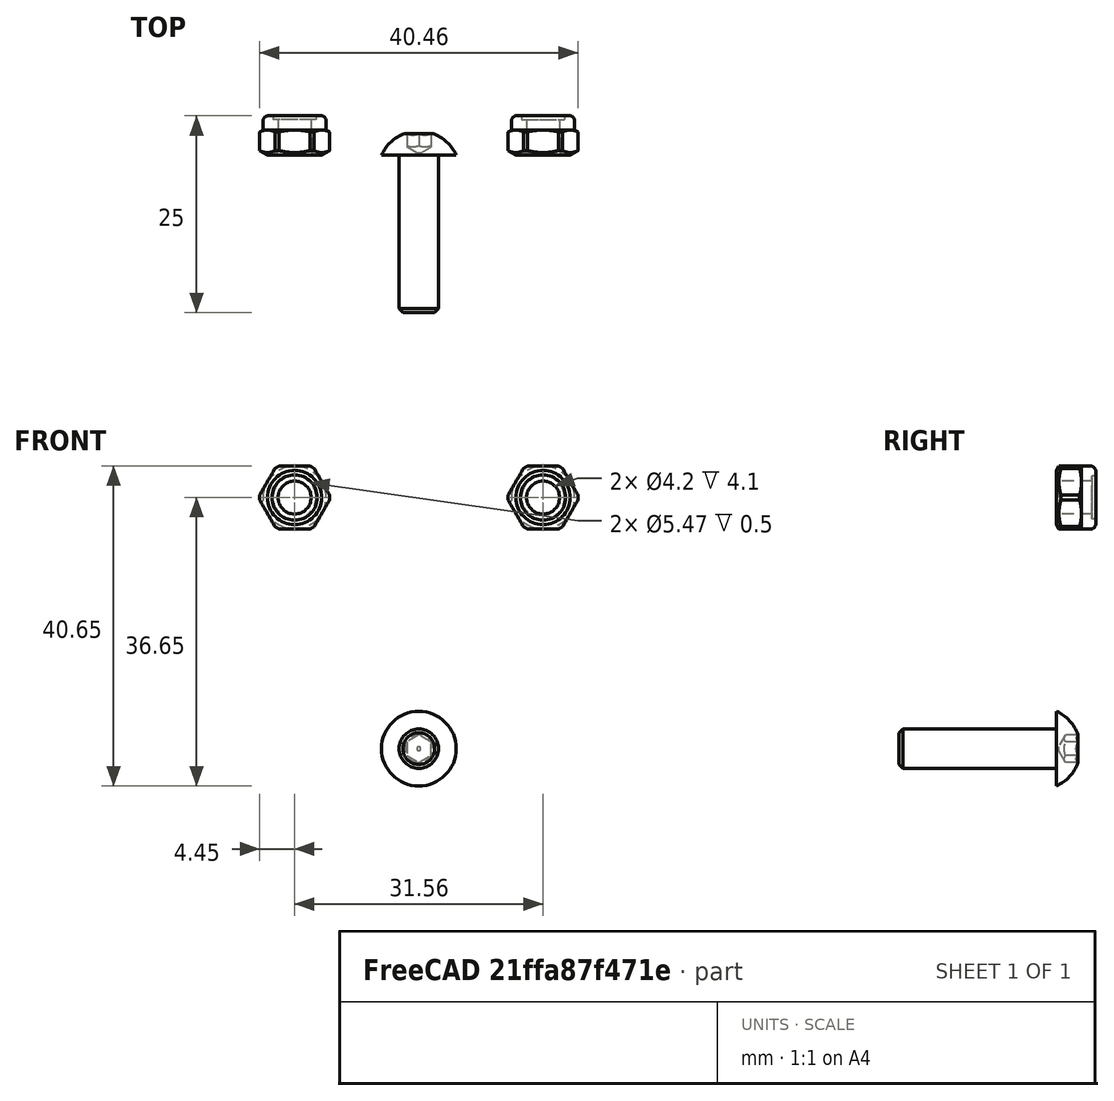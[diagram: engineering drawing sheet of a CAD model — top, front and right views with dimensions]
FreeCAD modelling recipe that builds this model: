
FCSTD DOCUMENT  (FreeCAD 0.19R24267 (Git))
Label: watercooled_print_head
License: All rights reserved
LicenseURL: http://en.wikipedia.org/wiki/All_rights_reserved
objects: App::Link×26, Part::FeaturePython×3, App::DocumentObjectGroup×2, PartDesign::CoordinateSystem×2, App::FeaturePython×1, App::Part×1
note: 5 computed .brp shape members not serialized (recipe doc carries the construction recipe); baked Part::Feature solids carry a one-line shape summary decoded from their .brp
EXTERNAL_REF file=watercooled_block.FCStd obj=LCS_7
EXTERNAL_REF file=watercooled_block.FCStd obj=Part
EXTERNAL_REF file=barb_fitting LC-0640-M6.FCStd obj=LCS_1
EXTERNAL_REF file=watercooled_block.FCStd obj=LCS_4
EXTERNAL_REF file=barb_fitting LC-0640-M6.FCStd obj=Part
EXTERNAL_REF file=watercooled_block.FCStd obj=LCS_5
EXTERNAL_REF file=eccentric_spacer.FCStd obj=LCS_1
EXTERNAL_REF file=watercooled_block.FCStd obj=LCS_9
EXTERNAL_REF file=eccentric_spacer.FCStd obj=Part
EXTERNAL_REF file=watercooled_block.FCStd obj=LCS_10
EXTERNAL_REF file=plug_fitting_MSWZ6.FCStd obj=LCS_1
EXTERNAL_REF file=watercooled_block.FCStd obj=LCS_3
EXTERNAL_REF file=plug_fitting_MSWZ6.FCStd obj=Part
EXTERNAL_REF file=e3d_volcano_assembly.FCStd obj=LCS_Origin
EXTERNAL_REF file=e3d_volcano_assembly.FCStd obj=Model
EXTERNAL_REF file=G5_extruder.FCStd obj=LCS_5
EXTERNAL_REF file=watercooled_block.FCStd obj=LCS_6
EXTERNAL_REF file=G5_extruder.FCStd obj=Model
EXTERNAL_REF file=eccentric_spacer.FCStd obj=LCS_2
EXTERNAL_REF file=precision_spacer.FCStd obj=LCS_2
EXTERNAL_REF file=precision_spacer.FCStd obj=Part
EXTERNAL_REF file=105zz_ball_bearing.FCStd obj=LCS_2
EXTERNAL_REF file=precision_spacer.FCStd obj=LCS_1
EXTERNAL_REF file=105zz_ball_bearing.FCStd obj=_05zz_ball_bearing
EXTERNAL_REF file=105zz_ball_bearing.FCStd obj=LCS_1
EXTERNAL_REF file=micro_v_wheel.FCStd obj=LCS_2
EXTERNAL_REF file=micro_v_wheel.FCStd obj=delrin_wheel
EXTERNAL_REF file=micro_v_wheel.FCStd obj=LCS_1
EXTERNAL_REF file=Aluminum Spacer 6mm002.FCStd obj=LCS_1
EXTERNAL_REF file=watercooled_block.FCStd obj=LCS_8
EXTERNAL_REF file=Aluminum Spacer 6mm002.FCStd obj=Aluminum_Spacer_6mm002
EXTERNAL_REF file=Aluminum Spacer 6mm002.FCStd obj=LCS_2
EXTERNAL_REF file=barb_fitting LC-0640-M6.FCStd obj=LCS_2
EXTERNAL_REF file=silicone_tube.FCStd obj=LCS_1
EXTERNAL_REF file=silicone_tube.FCStd obj=Part
EXTERNAL_REF file=openbuilds_low_profile_screws.FCStd obj=LCS_0
EXTERNAL_REF file=watercooled_block.FCStd obj=LCS_1
EXTERNAL_REF file=openbuilds_low_profile_screws.FCStd obj=low_profile_screw_l25mm
EXTERNAL_REF file=watercooled_block.FCStd obj=LCS_2
EXTERNAL_REF file=part_cooling_duct.FCStd obj=Part

FEATURE [App::DocumentObjectGroup] Parts
FEATURE [PartDesign::CoordinateSystem] LCS_Origin
  AttacherType = Attacher::AttachEngine3D
  MapMode = 2
  Support = -> [X_Axis]
FEATURE [App::DocumentObjectGroup] Constraints
FEATURE [App::FeaturePython] Variables  # WARN: FeaturePython — macro-defined, semantics opaque (R4)
FEATURE [App::Link] watercooled_block_watercooled_block
  AssemblyType = Asm4EE
  AttachedBy = #LCS_7
  AttachedTo = Parent Assembly#LCS_Origin
  AttachmentOffset = pos=(0,0,0) rot=(1,0,0;3.14159rad)
  LinkPlacement = pos=(6,3.3e-15,2.6e-15) rot=(0,0,-1;1.5708rad)
  LinkedObject = -> <external watercooled_block.FCStd>#Part
  Placement = pos=(6,3.3e-15,2.6e-15) rot=(0,0,-1;1.5708rad)
  expr: Placement = LCS_Origin.Placement * AttachmentOffset * watercooled_block#LCS_7.Placement ^ -1
FEATURE [App::Link] barb_fitting_LC_0640_M6_barb_fitting_LC_0640_M6  label="barb_fitting_LC_0640_M6_barb_fitting LC-0640-M6"
  AssemblyType = Asm4EE
  AttachedBy = #LCS_1
  AttachedTo = watercooled_block_watercooled_block#LCS_4
  LinkPlacement = pos=(14,-6.35,5.5) rot=(0.57735,0.57735,0.57735;2.0944rad)
  LinkedObject = -> <external barb_fitting LC-0640-M6.FCStd>#Part
  Placement = pos=(14,-6.35,5.5) rot=(0.57735,0.57735,0.57735;2.0944rad)
  expr: Placement = watercooled_block_watercooled_block.Placement * watercooled_block#LCS_4.Placement * AttachmentOffset * barb_fitting_LC_0640_M6#LCS_1.Placement ^ -1
FEATURE [App::Link] barb_fitting_LC_0640_M6_barb_fitting_LC_0640_M6001  label="barb_fitting_LC_0640_M6_barb_fitting LC-0640-M007"
  AssemblyType = Asm4EE
  AttachedBy = #LCS_1
  AttachedTo = watercooled_block_watercooled_block#LCS_5
  LinkPlacement = pos=(14,6.35,5.5) rot=(0.57735,0.57735,0.57735;2.0944rad)
  LinkedObject = -> <external barb_fitting LC-0640-M6.FCStd>#Part
  Placement = pos=(14,6.35,5.5) rot=(0.57735,0.57735,0.57735;2.0944rad)
  expr: Placement = watercooled_block_watercooled_block.Placement * watercooled_block#LCS_5.Placement * AttachmentOffset * barb_fitting_LC_0640_M6#LCS_1.Placement ^ -1
FEATURE [App::Link] eccentric_spacer_eccentric_spacer
  AssemblyType = Asm4EE
  AttachedBy = #LCS_1
  AttachedTo = watercooled_block_watercooled_block#LCS_9
  AttachmentOffset = pos=(0,0,0) rot=(0.707107,-0.707107,0;3.14159rad)
  LinkPlacement = pos=(-9,18.35,40.95) rot=(0.57735,0.57735,0.57735;4.18879rad)
  LinkedObject = -> <external eccentric_spacer.FCStd>#Part
  Placement = pos=(-9,18.35,40.95) rot=(0.57735,0.57735,0.57735;4.18879rad)
  expr: Placement = watercooled_block_watercooled_block.Placement * watercooled_block#LCS_9.Placement * AttachmentOffset * eccentric_spacer#LCS_1.Placement ^ -1
FEATURE [App::Link] eccentric_spacer_eccentric_spacer_2
  AssemblyType = Asm4EE
  AttachedBy = #LCS_1
  AttachedTo = watercooled_block_watercooled_block#LCS_10
  AttachmentOffset = pos=(0,0,0) rot=(0.707107,0.707107,0;3.14159rad)
  LinkPlacement = pos=(21,18.35,40.95) rot=(0.57735,-0.57735,-0.57735;4.18879rad)
  LinkedObject = -> <external eccentric_spacer.FCStd>#Part
  Placement = pos=(21,18.35,40.95) rot=(0.57735,-0.57735,-0.57735;4.18879rad)
  expr: Placement = watercooled_block_watercooled_block.Placement * watercooled_block#LCS_10.Placement * AttachmentOffset * eccentric_spacer#LCS_1.Placement ^ -1
FEATURE [App::Link] plug_fitting_MSWZ6_plug_fitting_MSWZ6
  AssemblyType = Asm4EE
  AttachedBy = #LCS_1
  AttachedTo = watercooled_block_watercooled_block#LCS_3
  AttachmentOffset = pos=(0,0,0) rot=(1,0,0;3.14159rad)
  LinkPlacement = pos=(-10,14.35,5.5) rot=(0.57735,-0.57735,-0.57735;2.0944rad)
  LinkedObject = -> <external plug_fitting_MSWZ6.FCStd>#Part
  Placement = pos=(-10,14.35,5.5) rot=(0.57735,-0.57735,-0.57735;2.0944rad)
  expr: Placement = watercooled_block_watercooled_block.Placement * watercooled_block#LCS_3.Placement * AttachmentOffset * plug_fitting_MSWZ6#LCS_1.Placement ^ -1
FEATURE [App::Link] e3d_volcano_assembly
  AssemblyType = Asm4EE
  AttachedBy = #LCS_Origin
  AttachedTo = watercooled_block_watercooled_block#LCS_7
  AttachmentOffset = pos=(0,0,0) rot=(1,0,0;3.14159rad)
  LinkPlacement = pos=(0,6e-16,0) rot=(0,0,1;0rad)
  LinkedObject = -> <external e3d_volcano_assembly.FCStd>#Model
  Placement = pos=(0,6e-16,0) rot=(0,0,1;0rad)
  expr: Placement = watercooled_block_watercooled_block.Placement * watercooled_block#LCS_7.Placement * AttachmentOffset * e3d_volcano_assembly#LCS_Origin.Placement ^ -1
FEATURE [App::Link] G5_extruder
  AssemblyType = Asm4EE
  AttachedBy = #LCS_5
  AttachedTo = watercooled_block_watercooled_block#LCS_6
  AttachmentOffset = pos=(0,0,0) rot=(0.707107,-0.707107,0;3.14159rad)
  LinkPlacement = pos=(-0.02386,0.00620281,15) rot=(0,0,-1;1.5708rad)
  LinkedObject = -> <external G5_extruder.FCStd>#Model
  Placement = pos=(-0.02386,0.00620281,15) rot=(0,0,-1;1.5708rad)
  expr: Placement = watercooled_block_watercooled_block.Placement * watercooled_block#LCS_6.Placement * AttachmentOffset * G5_extruder#LCS_5.Placement ^ -1
FEATURE [App::Link] precision_spacer_precision_spacer
  AssemblyType = Asm4EE
  AttachedBy = #LCS_2
  AttachedTo = eccentric_spacer_eccentric_spacer#LCS_2
  LinkPlacement = pos=(-9.78,24.35,40.95) rot=(0.57735,0.57735,0.57735;4.18879rad)
  LinkedObject = -> <external precision_spacer.FCStd>#Part
  Placement = pos=(-9.78,24.35,40.95) rot=(0.57735,0.57735,0.57735;4.18879rad)
  expr: Placement = eccentric_spacer_eccentric_spacer.Placement * eccentric_spacer#LCS_2.Placement * AttachmentOffset * precision_spacer#LCS_2.Placement ^ -1
FEATURE [App::Link] precision_spacer_precision_spacer_2
  AssemblyType = Asm4EE
  AttachedBy = #LCS_2
  AttachedTo = eccentric_spacer_eccentric_spacer_2#LCS_2
  LinkPlacement = pos=(21.78,24.35,40.95) rot=(0.57735,-0.57735,-0.57735;4.18879rad)
  LinkedObject = -> <external precision_spacer.FCStd>#Part
  Placement = pos=(21.78,24.35,40.95) rot=(0.57735,-0.57735,-0.57735;4.18879rad)
  expr: Placement = eccentric_spacer_eccentric_spacer_2.Placement * eccentric_spacer#LCS_2.Placement * AttachmentOffset * precision_spacer#LCS_2.Placement ^ -1
FEATURE [App::Link] _05zz_ball_bearing_105zz_ball_bearing
  AssemblyType = Asm4EE
  AttachedBy = #LCS_2
  AttachedTo = precision_spacer_precision_spacer#LCS_1
  LinkPlacement = pos=(-9.78,25.35,40.95) rot=(0,0,-1;4.71239rad)
  LinkedObject = -> <external 105zz_ball_bearing.FCStd>#_05zz_ball_bearing
  Placement = pos=(-9.78,25.35,40.95) rot=(0,0,-1;4.71239rad)
  expr: Placement = precision_spacer_precision_spacer.Placement * precision_spacer#LCS_1.Placement * AttachmentOffset * _05zz_ball_bearing#LCS_2.Placement ^ -1
FEATURE [App::Link] _05zz_ball_bearing_105zz_ball_bearing_2
  AssemblyType = Asm4EE
  AttachedBy = #LCS_2
  AttachedTo = precision_spacer_precision_spacer_2#LCS_1
  LinkPlacement = pos=(21.78,25.35,40.95) rot=(-0.707107,-0.707107,0;3.14159rad)
  LinkedObject = -> <external 105zz_ball_bearing.FCStd>#_05zz_ball_bearing
  Placement = pos=(21.78,25.35,40.95) rot=(-0.707107,-0.707107,0;3.14159rad)
  expr: Placement = precision_spacer_precision_spacer_2.Placement * precision_spacer#LCS_1.Placement * AttachmentOffset * _05zz_ball_bearing#LCS_2.Placement ^ -1
FEATURE [App::Link] micro_v_wheel_micro_v_wheel
  AssemblyType = Asm4EE
  AttachedBy = #LCS_2
  AttachedTo = _05zz_ball_bearing_105zz_ball_bearing#LCS_1
  LinkPlacement = pos=(-9.78,25.45,40.95) rot=(0,0,1;1.5708rad)
  LinkedObject = -> <external micro_v_wheel.FCStd>#delrin_wheel
  Placement = pos=(-9.78,25.45,40.95) rot=(0,0,1;1.5708rad)
  expr: Placement = _05zz_ball_bearing_105zz_ball_bearing.Placement * _05zz_ball_bearing#LCS_1.Placement * AttachmentOffset * micro_v_wheel#LCS_2.Placement ^ -1
FEATURE [App::Link] micro_v_wheel_micro_v_wheel_2
  AssemblyType = Asm4EE
  AttachedBy = #LCS_2
  AttachedTo = _05zz_ball_bearing_105zz_ball_bearing_2#LCS_1
  LinkPlacement = pos=(21.78,25.45,40.95) rot=(0.707107,0.707107,0;3.14159rad)
  LinkedObject = -> <external micro_v_wheel.FCStd>#delrin_wheel
  Placement = pos=(21.78,25.45,40.95) rot=(0.707107,0.707107,0;3.14159rad)
  expr: Placement = _05zz_ball_bearing_105zz_ball_bearing_2.Placement * _05zz_ball_bearing#LCS_1.Placement * AttachmentOffset * micro_v_wheel#LCS_2.Placement ^ -1
FEATURE [App::Link] _05zz_ball_bearing_105zz_ball_bearing001
  AssemblyType = Asm4EE
  AttachedBy = #LCS_2
  AttachedTo = micro_v_wheel_micro_v_wheel#LCS_1
  LinkPlacement = pos=(-9.78,30.35,40.95) rot=(0,0,-1;4.71239rad)
  LinkedObject = -> <external 105zz_ball_bearing.FCStd>#_05zz_ball_bearing
  Placement = pos=(-9.78,30.35,40.95) rot=(0,0,-1;4.71239rad)
  expr: Placement = micro_v_wheel_micro_v_wheel.Placement * micro_v_wheel#LCS_1.Placement * AttachmentOffset * _05zz_ball_bearing#LCS_2.Placement ^ -1
FEATURE [App::Link] _05zz_ball_bearing_105zz_ball_bearing002
  AssemblyType = Asm4EE
  AttachedBy = #LCS_2
  AttachedTo = micro_v_wheel_micro_v_wheel_2#LCS_1
  LinkPlacement = pos=(21.78,30.35,40.95) rot=(-0.707107,-0.707107,0;3.14159rad)
  LinkedObject = -> <external 105zz_ball_bearing.FCStd>#_05zz_ball_bearing
  Placement = pos=(21.78,30.35,40.95) rot=(-0.707107,-0.707107,0;3.14159rad)
  expr: Placement = micro_v_wheel_micro_v_wheel_2.Placement * micro_v_wheel#LCS_1.Placement * AttachmentOffset * _05zz_ball_bearing#LCS_2.Placement ^ -1
FEATURE [Part::FeaturePython] Nut  label="M5-Nut"  # Fasteners workbench fastener (typed FeaturePython)
  AssemblyType = Asm4EE
  AttachedBy = Origin
  AttachedTo = _05zz_ball_bearing_105zz_ball_bearing001#LCS_1
  Placement = pos=(-9.78,34.35,40.95) rot=(-1,0,0;1.5708rad)
  diameter = 3
  invert = false
  matchOuter = false
  offset = 0
  thread = false
  type = 5
  expr: Placement = _05zz_ball_bearing_105zz_ball_bearing001.Placement * _05zz_ball_bearing#LCS_1.Placement * AttachmentOffset
FEATURE [Part::FeaturePython] Nut001  label="M5-Nut001"  # Fasteners workbench fastener (typed FeaturePython)
  AssemblyType = Asm4EE
  AttachedBy = Origin
  AttachedTo = _05zz_ball_bearing_105zz_ball_bearing002#LCS_1
  Placement = pos=(21.78,34.35,40.95) rot=(0,0.707107,0.707107;3.14159rad)
  diameter = 3
  invert = false
  matchOuter = false
  offset = 0
  thread = false
  type = 5
  expr: Placement = _05zz_ball_bearing_105zz_ball_bearing002.Placement * _05zz_ball_bearing#LCS_1.Placement * AttachmentOffset
FEATURE [App::Link] Aluminum_Spacer_6mm002_Aluminum_Spacer_6mm002
  AssemblyType = Asm4EE
  AttachedBy = #LCS_1
  AttachedTo = watercooled_block_watercooled_block#LCS_8
  LinkPlacement = pos=(6,24.35,9.05) rot=(0,0.707107,-0.707107;3.14159rad)
  LinkedObject = -> <external Aluminum Spacer 6mm002.FCStd>#Aluminum_Spacer_6mm002
  Placement = pos=(6,24.35,9.05) rot=(0,0.707107,-0.707107;3.14159rad)
  expr: Placement = watercooled_block_watercooled_block.Placement * watercooled_block#LCS_8.Placement * AttachmentOffset * Aluminum_Spacer_6mm002#LCS_1.Placement ^ -1
FEATURE [App::Link] precision_spacer_precision_spacer001
  AssemblyType = Asm4EE
  AttachedBy = #LCS_1
  AttachedTo = Aluminum_Spacer_6mm002_Aluminum_Spacer_6mm002#LCS_2
  LinkPlacement = pos=(6,25.35,9.05) rot=(-1,0,0;4.71239rad)
  LinkedObject = -> <external precision_spacer.FCStd>#Part
  Placement = pos=(6,25.35,9.05) rot=(-1,0,0;4.71239rad)
  expr: Placement = Aluminum_Spacer_6mm002_Aluminum_Spacer_6mm002.Placement * Aluminum_Spacer_6mm002#LCS_2.Placement * AttachmentOffset * precision_spacer#LCS_1.Placement ^ -1
FEATURE [App::Link] _05zz_ball_bearing_105zz_ball_bearing003
  AssemblyType = Asm4EE
  AttachedBy = #LCS_1
  AttachedTo = precision_spacer_precision_spacer001#LCS_2
  LinkPlacement = pos=(6,29.35,9.05) rot=(-0.57735,0.57735,-0.57735;2.0944rad)
  LinkedObject = -> <external 105zz_ball_bearing.FCStd>#_05zz_ball_bearing
  Placement = pos=(6,29.35,9.05) rot=(-0.57735,0.57735,-0.57735;2.0944rad)
  expr: Placement = precision_spacer_precision_spacer001.Placement * precision_spacer#LCS_2.Placement * AttachmentOffset * _05zz_ball_bearing#LCS_1.Placement ^ -1
FEATURE [App::Link] micro_v_wheel_micro_v_wheel001
  AssemblyType = Asm4EE
  AttachedBy = #LCS_1
  AttachedTo = _05zz_ball_bearing_105zz_ball_bearing003#LCS_2
  LinkPlacement = pos=(6,34.25,9.05) rot=(0.57735,-0.57735,0.57735;4.18879rad)
  LinkedObject = -> <external micro_v_wheel.FCStd>#delrin_wheel
  Placement = pos=(6,34.25,9.05) rot=(0.57735,-0.57735,0.57735;4.18879rad)
  expr: Placement = _05zz_ball_bearing_105zz_ball_bearing003.Placement * _05zz_ball_bearing#LCS_2.Placement * AttachmentOffset * micro_v_wheel#LCS_1.Placement ^ -1
FEATURE [App::Link] _05zz_ball_bearing_105zz_ball_bearing004
  AssemblyType = Asm4EE
  AttachedBy = #LCS_1
  AttachedTo = micro_v_wheel_micro_v_wheel001#LCS_2
  LinkPlacement = pos=(6,34.35,9.05) rot=(-0.57735,0.57735,-0.57735;2.0944rad)
  LinkedObject = -> <external 105zz_ball_bearing.FCStd>#_05zz_ball_bearing
  Placement = pos=(6,34.35,9.05) rot=(-0.57735,0.57735,-0.57735;2.0944rad)
  expr: Placement = micro_v_wheel_micro_v_wheel001.Placement * micro_v_wheel#LCS_2.Placement * AttachmentOffset * _05zz_ball_bearing#LCS_1.Placement ^ -1
FEATURE [Part::FeaturePython] Screw  label="M5x20-Screw"  # Fasteners workbench fastener (typed FeaturePython)
  AssemblyType = Asm4EE
  AttachedBy = Origin
  AttachedTo = _05zz_ball_bearing_105zz_ball_bearing004#LCS_2
  AttachmentOffset = pos=(0,0,0) rot=(1,0,0;3.14159rad)
  Placement = pos=(6,34.35,9.05) rot=(0.57735,0.57735,0.57735;4.18879rad)
  diameter = 3
  invert = false
  length = 5
  lengthCustom = 20
  matchOuter = false
  offset = 0
  thread = false
  type = 38
  expr: Placement = _05zz_ball_bearing_105zz_ball_bearing004.Placement * _05zz_ball_bearing#LCS_2.Placement * AttachmentOffset
FEATURE [App::Link] silicone_tube_silicone_tube
  AssemblyType = Asm4EE
  AttachedBy = #LCS_1
  AttachedTo = barb_fitting_LC_0640_M6_barb_fitting_LC_0640_M6#LCS_2
  AttachmentOffset = pos=(0,0,0) rot=(0,1,0;3.14159rad)
  LinkPlacement = pos=(21.3,-6.35,5.5) rot=(0,0,1;4.71239rad)
  LinkedObject = -> <external silicone_tube.FCStd>#Part
  Placement = pos=(21.3,-6.35,5.5) rot=(0,0,1;4.71239rad)
  expr: Placement = barb_fitting_LC_0640_M6_barb_fitting_LC_0640_M6.Placement * barb_fitting_LC_0640_M6#LCS_2.Placement * AttachmentOffset * silicone_tube#LCS_1.Placement ^ -1
FEATURE [App::Link] silicone_tube_silicone_tube_2
  AssemblyType = Asm4EE
  AttachedBy = #LCS_1
  AttachedTo = barb_fitting_LC_0640_M6_barb_fitting_LC_0640_M6001#LCS_2
  AttachmentOffset = pos=(0,0,0) rot=(0,-1,0;3.14159rad)
  LinkPlacement = pos=(21.3,6.35,5.5) rot=(0,0,-1;1.5708rad)
  LinkedObject = -> <external silicone_tube.FCStd>#Part
  Placement = pos=(21.3,6.35,5.5) rot=(0,0,-1;1.5708rad)
  expr: Placement = barb_fitting_LC_0640_M6_barb_fitting_LC_0640_M6001.Placement * barb_fitting_LC_0640_M6#LCS_2.Placement * AttachmentOffset * silicone_tube#LCS_1.Placement ^ -1
FEATURE [App::Link] openbuilds_low_profile_screws_low_profile_screw_l25mm
  AssemblyType = Asm4EE
  AttachedBy = #LCS_0
  AttachedTo = watercooled_block_watercooled_block#LCS_1
  AttachmentOffset = pos=(0,0,0) rot=(1,0,0;3.14159rad)
  LinkPlacement = pos=(-9,14.17,40.95) rot=(0,0,1;1.5708rad)
  LinkedObject = -> <external openbuilds_low_profile_screws.FCStd>#low_profile_screw_l25mm
  Placement = pos=(-9,14.17,40.95) rot=(0,0,1;1.5708rad)
  expr: Placement = watercooled_block_watercooled_block.Placement * watercooled_block#LCS_1.Placement * AttachmentOffset * openbuilds_low_profile_screws#LCS_0.Placement ^ -1
FEATURE [App::Link] openbuilds_low_profile_screws_low_profile_screw_l25mm001
  AssemblyType = Asm4EE
  AttachedBy = #LCS_0
  AttachedTo = watercooled_block_watercooled_block#LCS_2
  AttachmentOffset = pos=(0,0,0) rot=(1,0,0;3.14159rad)
  LinkPlacement = pos=(21,14.17,40.95) rot=(0,0,1;1.5708rad)
  LinkedObject = -> <external openbuilds_low_profile_screws.FCStd>#low_profile_screw_l25mm
  Placement = pos=(21,14.17,40.95) rot=(0,0,1;1.5708rad)
  expr: Placement = watercooled_block_watercooled_block.Placement * watercooled_block#LCS_2.Placement * AttachmentOffset * openbuilds_low_profile_screws#LCS_0.Placement ^ -1
FEATURE [PartDesign::CoordinateSystem] LCS_1
  AttacherType = Attacher::AttachEngine3D
  Placement = pos=(6,30,25) rot=(0,0,1;0rad)
FEATURE [App::Link] part_cooling_duct_part_cooling_duct
  LinkPlacement = pos=(26,-16,12) rot=(0,0,1;0rad)
  LinkedObject = -> <external part_cooling_duct.FCStd>#Part
  Placement = pos=(26,-16,12) rot=(0,0,1;0rad)
FEATURE [App::Part] Model
  Configuration = 0
  Group = -> [LCS_Origin,Constraints,Variables,watercooled_block_watercooled_block,barb_fitting_LC_0640_M6_barb_fitting_LC_0640_M6,barb_fitting_LC_0640_M6_barb_fitting_LC_0640_M6001,eccentric_spacer_eccentric_spacer,eccentric_spacer_eccentric_spacer_2,plug_fitting_MSWZ6_plug_fitting_MSWZ6,e3d_volcano_assembly,G5_extruder,precision_spacer_precision_spacer,precision_spacer_precision_spacer_2,+20 more]
  Origin = -> Origin
  Type = Assembly4 Model

RESOLVED EXTERNAL PARTS (link-assembly join: the EXTERNAL_REF files above that resolve inside this repo's crawl, each included once):
---- part G5_extruder.FCStd = doc fcstd_53e58183142c ----
FCSTD DOCUMENT  (FreeCAD 0.19R24267 (Git))
Label: G5_extruder
License: All rights reserved
LicenseURL: http://en.wikipedia.org/wiki/All_rights_reserved
objects: Part::FeaturePython×6, App::Link×4, PartDesign::CoordinateSystem×2, App::DocumentObjectGroup×2, App::FeaturePython×1, App::Part×1
note: 8 computed .brp shape members not serialized (recipe doc carries the construction recipe); baked Part::Feature solids carry a one-line shape summary decoded from their .brp
EXTERNAL_REF file=G5_BASE.FCStd obj=LCS_1
EXTERNAL_REF file=G5_BASE.FCStd obj=Part
EXTERNAL_REF file=G5_BASE.FCStd obj=LCS_2
EXTERNAL_REF file=G5_TOP.FCStd obj=LCS_1
EXTERNAL_REF file=G5_TOP.FCStd obj=Part
EXTERNAL_REF file=G5_CAP.FCStd obj=LCS_1
EXTERNAL_REF file=G5_TOP.FCStd obj=LCS_2
EXTERNAL_REF file=G5_CAP.FCStd obj=Part
EXTERNAL_REF file=G5_BASE.FCStd obj=LCS_3
EXTERNAL_REF file=G5_TENSIONER.FCStd obj=LCS_1
EXTERNAL_REF file=G5_TENSIONER.FCStd obj=Part
EXTERNAL_REF file=G5_CAP.FCStd obj=LCS_4
EXTERNAL_REF file=G5_CAP.FCStd obj=LCS_3
EXTERNAL_REF file=G5_CAP.FCStd obj=LCS_2
EXTERNAL_REF file=G5_BASE.FCStd obj=LCS_4
EXTERNAL_REF file=G5_CAP.FCStd obj=LCS_5
EXTERNAL_REF file=G5_CAP.FCStd obj=LCS_6
EXTERNAL_REF file=G5_BASE.FCStd obj=LCS_5

FEATURE [PartDesign::CoordinateSystem] LCS_Origin
  AttacherType = Attacher::AttachEngine3D
  MapMode = 2
  Support = -> [X_Axis]
FEATURE [App::DocumentObjectGroup] Constraints
FEATURE [App::FeaturePython] Variables  # WARN: FeaturePython — macro-defined, semantics opaque (R4)
FEATURE [App::Link] G5_BASE_G5_BASE
  AssemblyType = Asm4EE
  AttachedBy = #LCS_1
  AttachedTo = Parent Assembly#LCS_Origin
  AttachmentOffset = pos=(0,0,0) rot=(0.707107,0.707107,0;3.14159rad)
  LinkPlacement = pos=(120,-8.89e-14,-0.0600001) rot=(0,0,1;0rad)
  LinkedObject = -> <external G5_BASE.FCStd>#Part
  Placement = pos=(120,-8.89e-14,-0.0600001) rot=(0,0,1;0rad)
  expr: Placement = LCS_Origin.Placement * AttachmentOffset * G5_BASE#LCS_1.Placement ^ -1
FEATURE [App::Link] G5_TOP_G5_TOP
  AssemblyType = Asm4EE
  AttachedBy = #LCS_1
  AttachedTo = G5_BASE_G5_BASE#LCS_2
  AttachmentOffset = pos=(0,0,0) rot=(0.707107,0.707107,0;3.14159rad)
  LinkPlacement = pos=(119.999,-2.82409e-05,-0.0599402) rot=(0,1,0;6.28318rad)
  LinkedObject = -> <external G5_TOP.FCStd>#Part
  Placement = pos=(119.999,-2.82409e-05,-0.0599402) rot=(0,1,0;6.28318rad)
  expr: Placement = G5_BASE_G5_BASE.Placement * G5_BASE#LCS_2.Placement * AttachmentOffset * G5_TOP#LCS_1.Placement ^ -1
FEATURE [App::Link] G5_CAP_G5_CAP
  AssemblyType = Asm4EE
  AttachedBy = #LCS_1
  AttachedTo = G5_TOP_G5_TOP#LCS_2
  AttachmentOffset = pos=(0,0,0) rot=(0,0,1;1.5708rad)
  LinkPlacement = pos=(120.005,-0.0748696,-0.0599954) rot=(-0.00069,-6.9e-05,1;6.28276rad)
  LinkedObject = -> <external G5_CAP.FCStd>#Part
  Placement = pos=(120.005,-0.0748696,-0.0599954) rot=(-0.00069,-6.9e-05,1;6.28276rad)
  expr: Placement = G5_TOP_G5_TOP.Placement * G5_TOP#LCS_2.Placement * AttachmentOffset * G5_CAP#LCS_1.Placement ^ -1
FEATURE [App::Link] G5_TENSIONER_G5_TENSIONER
  AssemblyType = Asm4EE
  AttachedBy = #LCS_1
  AttachedTo = G5_BASE_G5_BASE#LCS_3
  AttachmentOffset = pos=(0,0,0) rot=(-0.707107,-0.707107,0;3.14159rad)
  LinkPlacement = pos=(12.06,-34.3342,61.6058) rot=(0.57735,0.57735,-0.57735;4.18879rad)
  LinkedObject = -> <external G5_TENSIONER.FCStd>#Part
  Placement = pos=(12.06,-34.3342,61.6058) rot=(0.57735,0.57735,-0.57735;4.18879rad)
  expr: Placement = G5_BASE_G5_BASE.Placement * G5_BASE#LCS_3.Placement * AttachmentOffset * G5_TENSIONER#LCS_1.Placement ^ -1
FEATURE [Part::FeaturePython] Screw001  label="M2.5x30-Screw041"  # Fasteners workbench fastener (typed FeaturePython)
  AssemblyType = Asm4EE
  AttachedBy = Origin
  AttachedTo = G5_CAP_G5_CAP#LCS_4
  AttachmentOffset = pos=(0,0,0) rot=(0,-1,0;3.14159rad)
  Placement = pos=(5.25469,13.8071,25.84) rot=(0,0,1;3.14117rad)
  diameter = 3
  invert = false
  length = 10
  lengthCustom = 30
  matchOuter = false
  offset = 0
  thread = false
  type = 32
  expr: Placement = G5_CAP_G5_CAP.Placement * G5_CAP#LCS_4.Placement * AttachmentOffset
FEATURE [Part::FeaturePython] Screw002  label="M2.5x30-Screw042"  # Fasteners workbench fastener (typed FeaturePython)
  AssemblyType = Asm4EE
  AttachedBy = Origin
  AttachedTo = G5_CAP_G5_CAP#LCS_3
  AttachmentOffset = pos=(0,0,0) rot=(0,0,1;3.14159rad)
  Placement = pos=(-4.75709,-14.2647,25.84) rot=(0,0,-1;1.57122rad)
  diameter = 3
  invert = false
  length = 10
  lengthCustom = 30
  matchOuter = false
  offset = 0
  thread = false
  type = 32
  expr: Placement = G5_CAP_G5_CAP.Placement * G5_CAP#LCS_3.Placement * AttachmentOffset
FEATURE [Part::FeaturePython] Screw003  label="M2.5x30-Screw"  # Fasteners workbench fastener (typed FeaturePython)
  AssemblyType = Asm4EE
  AttachedBy = Origin
  AttachedTo = G5_CAP_G5_CAP#LCS_2
  AttachmentOffset = pos=(0,0,0) rot=(0,0,1;3.14159rad)
  Placement = pos=(15.5062,2.07386,25.84) rot=(0,0,-1;3.14159rad)
  diameter = 3
  invert = false
  length = 10
  lengthCustom = 30
  matchOuter = false
  offset = 0
  thread = false
  type = 32
  expr: Placement = G5_CAP_G5_CAP.Placement * G5_CAP#LCS_2.Placement * AttachmentOffset
FEATURE [Part::FeaturePython] Screw004  label="M2x10-Screw"  # Fasteners workbench fastener (typed FeaturePython)
  AssemblyType = Asm4EE
  AttachedBy = Origin
  AttachedTo = G5_BASE_G5_BASE#LCS_4
  Placement = pos=(-5.75,12.6658,12.94) rot=(0.707107,0,-0.707107;3.14159rad)
  diameter = 2
  invert = false
  length = 5
  lengthCustom = 10
  matchOuter = false
  offset = 0
  thread = false
  type = 32
  expr: Placement = G5_BASE_G5_BASE.Placement * G5_BASE#LCS_4.Placement * AttachmentOffset
FEATURE [Part::FeaturePython] Screw005  label="M2.5x10-Screw"  # Fasteners workbench fastener (typed FeaturePython)
  AssemblyType = Asm4EE
  AttachedBy = Origin
  AttachedTo = G5_CAP_G5_CAP#LCS_5
  AttachmentOffset = pos=(0,0,0) rot=(0,1,0;3.14159rad)
  Placement = pos=(13.505,1.63524,37.8722) rot=(-0.000211,-1,0.000211;4.71239rad)
  diameter = 3
  invert = false
  length = 4
  lengthCustom = 10
  matchOuter = false
  offset = 0
  thread = false
  type = 32
  expr: Placement = G5_CAP_G5_CAP.Placement * G5_CAP#LCS_5.Placement * AttachmentOffset
FEATURE [Part::FeaturePython] Nut  label="M2.5-Nut"  # Fasteners workbench fastener (typed FeaturePython)
  AssemblyType = Asm4EE
  AttachedBy = Origin
  AttachedTo = G5_CAP_G5_CAP#LCS_6
  Placement = pos=(6.49955,1.6382,37.8722) rot=(0.000211,1,0.000211;4.71239rad)
  diameter = 3
  invert = false
  matchOuter = false
  offset = 0
  thread = false
  type = 7
  expr: Placement = G5_CAP_G5_CAP.Placement * G5_CAP#LCS_6.Placement * AttachmentOffset
FEATURE [App::DocumentObjectGroup] Group  label="Fasteners"
  Group = -> [Screw004,Screw003,Screw002,Screw001,Screw005,Nut]
FEATURE [PartDesign::CoordinateSystem] LCS_5
  AttacherType = Attacher::AttachEngine3D
  Placement = pos=(15.5062,2.07386,-3.88e-14) rot=(1,0,0;3.14159rad)
  expr: Placement = G5_BASE_G5_BASE.Placement * G5_BASE#LCS_5.Placement * AttachmentOffset
FEATURE [App::Part] Model
  Configuration = 0
  Group = -> [LCS_Origin,Constraints,Variables,G5_BASE_G5_BASE,G5_TOP_G5_TOP,G5_CAP_G5_CAP,G5_TENSIONER_G5_TENSIONER,Screw003,Screw004,Screw001,Screw002,Group,Screw005,Nut,LCS_5]
  Origin = -> Origin
  Type = Assembly4 Model
---- part e3d_volcano_assembly.FCStd = doc fcstd_a8c63eb28e12 ----
FCSTD DOCUMENT  (FreeCAD 0.19R24267 (Git))
Label: e3d_volcano_assembly
License: All rights reserved
LicenseURL: http://en.wikipedia.org/wiki/All_rights_reserved
objects: App::Link×4, Part::FeaturePython×3, App::DocumentObjectGroup×2, PartDesign::CoordinateSystem×1, App::FeaturePython×1, App::Part×1
note: 4 computed .brp shape members not serialized (recipe doc carries the construction recipe); baked Part::Feature solids carry a one-line shape summary decoded from their .brp
EXTERNAL_REF file=volcano_heat_break.FCStd obj=LCS_1
EXTERNAL_REF file=volcano_heat_break.FCStd obj=Part
EXTERNAL_REF file=volcano_heat_break.FCStd obj=LCS_3
EXTERNAL_REF file=volcano_nozzle.FCStd obj=LCS_1
EXTERNAL_REF file=volcano_nozzle.FCStd obj=Part
EXTERNAL_REF file=Volcano_Heater_Block.FCStd obj=LCS_1
EXTERNAL_REF file=volcano_heat_break.FCStd obj=LCS_2
EXTERNAL_REF file=Volcano_Heater_Block.FCStd obj=Part
EXTERNAL_REF file=Volcano_Heater_Block.FCStd obj=LCS_3
EXTERNAL_REF file=heater_cartridge.FCStd obj=LCS_1
EXTERNAL_REF file=heater_cartridge.FCStd obj=Part049
EXTERNAL_REF file=Volcano_Heater_Block.FCStd obj=LCS_4
EXTERNAL_REF file=Volcano_Heater_Block.FCStd obj=LCS_5
EXTERNAL_REF file=Volcano_Heater_Block.FCStd obj=LCS_6

FEATURE [App::DocumentObjectGroup] Parts
FEATURE [PartDesign::CoordinateSystem] LCS_Origin
  AttacherType = Attacher::AttachEngine3D
  MapMode = 2
  Support = -> [X_Axis]
FEATURE [App::DocumentObjectGroup] Constraints
FEATURE [App::FeaturePython] Variables  # WARN: FeaturePython — macro-defined, semantics opaque (R4)
FEATURE [App::Link] volcano_heat_break_volcano_heat_break
  AssemblyType = Asm4EE
  AttachedBy = #LCS_1
  AttachedTo = Parent Assembly#LCS_Origin
  AttachmentOffset = pos=(0,0,0) rot=(0,1,0;3.14159rad)
  LinkPlacement = pos=(50,-7.1e-15,-7.75) rot=(0,0,1;4.71239rad)
  LinkedObject = -> <external volcano_heat_break.FCStd>#Part
  Placement = pos=(50,-7.1e-15,-7.75) rot=(0,0,1;4.71239rad)
  expr: Placement = LCS_Origin.Placement * AttachmentOffset * volcano_heat_break#LCS_1.Placement ^ -1
FEATURE [App::Link] volcano_nozzle_volcano_nozzle
  AssemblyType = Asm4EE
  AttachedBy = #LCS_1
  AttachedTo = volcano_heat_break_volcano_heat_break#LCS_3
  AttachmentOffset = pos=(0,0,0) rot=(0,1,0;3.14159rad)
  LinkPlacement = pos=(2.2e-14,1.3e-15,-28.745) rot=(0,0,1;1.5708rad)
  LinkedObject = -> <external volcano_nozzle.FCStd>#Part
  Placement = pos=(2.2e-14,1.3e-15,-28.745) rot=(0,0,1;1.5708rad)
  expr: Placement = volcano_heat_break_volcano_heat_break.Placement * volcano_heat_break#LCS_3.Placement * AttachmentOffset * volcano_nozzle#LCS_1.Placement ^ -1
FEATURE [App::Link] Volcano_Heater_Block_Volcano_Heater_Block
  AssemblyType = Asm4EE
  AttachedBy = #LCS_1
  AttachedTo = volcano_heat_break_volcano_heat_break#LCS_2
  AttachmentOffset = pos=(0,0,0) rot=(0,0,1;3.14159rad)
  LinkPlacement = pos=(15.5,-7,-22.5) rot=(0,-0.707107,-0.707107;3.14159rad)
  LinkedObject = -> <external Volcano_Heater_Block.FCStd>#Part
  Placement = pos=(15.5,-7,-22.5) rot=(0,-0.707107,-0.707107;3.14159rad)
  expr: Placement = volcano_heat_break_volcano_heat_break.Placement * volcano_heat_break#LCS_2.Placement * AttachmentOffset * Volcano_Heater_Block#LCS_1.Placement ^ -1
FEATURE [App::Link] heater_cartridge_heater_cartridge
  AssemblyType = Asm4EE
  AttachedBy = #LCS_1
  AttachedTo = Volcano_Heater_Block_Volcano_Heater_Block#LCS_3
  LinkPlacement = pos=(7.5,0.5,-2.5) rot=(0,0,1;6.28279rad)
  LinkedObject = -> <external heater_cartridge.FCStd>#Part049
  Placement = pos=(7.5,0.5,-2.5) rot=(0,0,1;6.28279rad)
  expr: Placement = Volcano_Heater_Block_Volcano_Heater_Block.Placement * Volcano_Heater_Block#LCS_3.Placement * AttachmentOffset * heater_cartridge#LCS_1.Placement ^ -1
FEATURE [Part::FeaturePython] Screw  label="M3x10-Screw"  # Fasteners workbench fastener (typed FeaturePython)
  AssemblyType = Asm4EE
  AttachedBy = Origin
  AttachedTo = Volcano_Heater_Block_Volcano_Heater_Block#LCS_4
  Placement = pos=(13,4.5,-7.5) rot=(-0.57735,-0.57735,-0.57735;2.0944rad)
  diameter = 1
  invert = false
  length = 2
  lengthCustom = 10
  matchOuter = false
  offset = 0
  thread = false
  type = 38
  expr: Placement = Volcano_Heater_Block_Volcano_Heater_Block.Placement * Volcano_Heater_Block#LCS_4.Placement * AttachmentOffset
FEATURE [Part::FeaturePython] Screw001  label="M3x10-Screw001"  # Fasteners workbench fastener (typed FeaturePython)
  AssemblyType = Asm4EE
  AttachedBy = Origin
  AttachedTo = Volcano_Heater_Block_Volcano_Heater_Block#LCS_5
  Placement = pos=(13,4.5,-17) rot=(-0.57735,-0.57735,-0.57735;2.0944rad)
  diameter = 1
  invert = false
  length = 2
  lengthCustom = 10
  matchOuter = false
  offset = 0
  thread = false
  type = 38
  expr: Placement = Volcano_Heater_Block_Volcano_Heater_Block.Placement * Volcano_Heater_Block#LCS_5.Placement * AttachmentOffset
FEATURE [Part::FeaturePython] Screw002  label="M3x5-Screw"  # Fasteners workbench fastener (typed FeaturePython)
  AssemblyType = Asm4EE
  AttachedBy = Origin
  AttachedTo = Volcano_Heater_Block_Volcano_Heater_Block#LCS_6
  Placement = pos=(-5.5,4.5,-12.5) rot=(-0.57735,-0.57735,-0.57735;2.0944rad)
  diameter = 6
  invert = false
  length = 3
  lengthCustom = 5
  matchOuter = false
  offset = 0
  thread = false
  type = 31
  expr: Placement = Volcano_Heater_Block_Volcano_Heater_Block.Placement * Volcano_Heater_Block#LCS_6.Placement * AttachmentOffset
FEATURE [App::Part] Model
  Configuration = 0
  Group = -> [LCS_Origin,Constraints,Variables,volcano_heat_break_volcano_heat_break,volcano_nozzle_volcano_nozzle,Volcano_Heater_Block_Volcano_Heater_Block,heater_cartridge_heater_cartridge,Screw,Screw001,Screw002]
  Origin = -> Origin
  Type = Assembly4 Model
---- part openbuilds_low_profile_screws.FCStd = doc fcstd_c06f41d2da36 ----
FCSTD DOCUMENT  (FreeCAD 0.19R24267 (Git))
Label: openbuilds_low_profile_screws
License: All rights reserved
LicenseURL: http://en.wikipedia.org/wiki/All_rights_reserved
objects: Sketcher::SketchObject×1, PartDesign::Revolution×1, PartDesign::SubtractivePrism×1, PartDesign::CoordinateSystem×1, PartDesign::Body×1, App::Part×1
note: 7 computed .brp shape members not serialized (recipe doc carries the construction recipe); baked Part::Feature solids carry a one-line shape summary decoded from their .brp

FEATURE [Sketcher::SketchObject] Sketch_002
  FullyConstrained = false
  sketch-geometry (9):
    g0: LineSegment StartX=-1.5 StartY=4.16144 StartZ=0 EndX=-1.5 EndY=1.75 EndZ=0
    g1: LineSegment StartX=0.25 StartY=0 StartZ=0 EndX=25 EndY=0 EndZ=0
    g2: LineSegment StartX=25 StartY=0 StartZ=0 EndX=25 EndY=1.9 EndZ=0
    g3: LineSegment StartX=25 StartY=1.9 StartZ=0 EndX=24.5 EndY=2.4 EndZ=0
    g4: LineSegment StartX=24.5 StartY=2.4 StartZ=0 EndX=0 EndY=2.4 EndZ=0
    g5: LineSegment StartX=0 StartY=2.4 StartZ=0 EndX=0 EndY=4.16144 EndZ=0
    g6: ArcOfCircle CenterX=-0.75 CenterY=3.5 CenterZ=0 NormalX=0 NormalY=0 NormalZ=1 AngleXU=0 Radius=1 StartAngle=0.722734 EndAngle=2.41886
    g7: GeomPoint X=-0.75 Y=4.5 Z=0
    g8: LineSegment StartX=-1.5 StartY=1.75 StartZ=0 EndX=0.25 EndY=0 EndZ=0
  constraints (27):
    c: PointOnObject(g1,g-1)
    c: Coincident(g1,g2)
    c: Coincident(g2,g3)
    c: Coincident(g3,g4)
    c: PointOnObject(g4,g-2)
    c: Horizontal(g4)
    c: Coincident(g4,g5)
    c: PointOnObject(g5,g-2)
    c: Vertical(g0)
    c: Coincident(g6,g0)
    c: Coincident(g6,g5)
    c: Horizontal(g0,g5)
    c: DistanceX(g0,g5) = 1.5
    c: PointOnObject(g7,g6)
    c: Vertical(g7,g6)
    c: Angle(g3,g2) = 2.35619
    c: Vertical(g2)
    c: DistanceY(g-1,g4) = 2.4
    c: DistanceY(g2,g3) = 0.5
    c: DistanceX(g-1,g1) = 25
    c: DistanceY(g-1,g6) = 3.5
    c: Coincident(g0,g8)
    c: Coincident(g1,g8)
    c: DistanceY(g-1,g7) = 4.5
    c: Angle(g8,g-1) = 0.785398
    c: DistanceY(g1,g0) = 1.75
    c: Horizontal(g1)
FEATURE [PartDesign::Revolution] Revolution
  Angle = 360
  Axis = (1,0,0)
  Base = (0,0,0)
  Profile = -> Sketch_002
  ReferenceAxis = -> Sketch_002 [H_Axis]
FEATURE [PartDesign::SubtractivePrism] Prism
  AttacherType = Attacher::AttachEngine3D
  BaseFeature = -> Revolution
  Circumradius = 1.73205
  FirstAngle = 0
  Height = 2.5
  MapMode = 11
  Placement = pos=(-1.5,0,0) rot=(0.707107,0,0.707107;3.14159rad)
  Polygon = 6
  SecondAngle = 0
  Support = -> [Revolution]
  expr: Circumradius = 3 / sqrt(3) * 1mm
FEATURE [PartDesign::CoordinateSystem] LCS_0
  AttacherType = Attacher::AttachEngine3D
  MapMode = 11
  Placement = pos=(0,0,0) rot=(0.707107,0,0.707107;3.14159rad)
  Support = -> [Prism]
FEATURE [PartDesign::Body] Body
  Group = -> [Sketch_002,Revolution,Prism]
  Origin = -> Origin001
  Tip = -> Prism
FEATURE [App::Part] low_profile_screw_l25mm
  Group = -> [LCS_0,Body]
  Origin = -> Origin
---- part part_cooling_duct.FCStd = doc fcstd_d8950f733f22 ----
FCSTD DOCUMENT  (FreeCAD 0.19R24267 (Git))
Label: part_cooling_duct
License: All rights reserved
LicenseURL: http://en.wikipedia.org/wiki/All_rights_reserved
objects: Sketcher::SketchObject×7, PartDesign::Body×5, PartDesign::Pad×3, PartDesign::Pocket×2, PartDesign::SubShapeBinder×2, PartDesign::AdditivePipe×2, App::Part×1
note: 28 computed .brp shape members not serialized (recipe doc carries the construction recipe); baked Part::Feature solids carry a one-line shape summary decoded from their .brp
EXTERNAL_REF file=watercooled_print_head.FCStd obj=Model

FEATURE [Sketcher::SketchObject] Sketch
  FullyConstrained = true
  MapMode = 5
  Placement = pos=(0,0,0) rot=(1,0,0;1.5708rad)
  Support = -> [XZ_Plane]
  sketch-geometry (9):
    g0: LineSegment StartX=0 StartY=0 StartZ=0 EndX=-50 EndY=0 EndZ=0
    g1: LineSegment StartX=-50 StartY=0 StartZ=0 EndX=-50 EndY=15 EndZ=0
    g2: LineSegment StartX=-50 StartY=15 StartZ=0 EndX=0 EndY=15 EndZ=0
    g3: LineSegment StartX=0 StartY=15 StartZ=0 EndX=0 EndY=0 EndZ=0
    g4: LineSegment StartX=0 StartY=0 StartZ=0 EndX=0 EndY=-30 EndZ=0
    g5: ArcOfCircle CenterX=-5 CenterY=-30 CenterZ=0 NormalX=0 NormalY=0 NormalZ=1 AngleXU=0 Radius=5 StartAngle=4.71239 EndAngle=6.28319
    g6: LineSegment StartX=-5 StartY=-35 StartZ=0 EndX=-35 EndY=-35 EndZ=0
    g7: LineSegment StartX=-35 StartY=-35 StartZ=0 EndX=-35 EndY=0 EndZ=0
    g8: LineSegment StartX=-35 StartY=0 StartZ=0 EndX=0 EndY=0 EndZ=0
  constraints (24):
    c: Coincident(g0,g1)
    c: Coincident(g1,g2)
    c: Coincident(g2,g3)
    c: Coincident(g3,g0)
    c: Horizontal(g0)
    c: Horizontal(g2)
    c: Vertical(g1)
    c: Vertical(g3)
    c: Coincident(g0,g-1)
    c: DistanceX(g2,g2) = 50
    c: DistanceY(g1,g1) = 15
    c: Tangent(g4,g5) = 1.5708
    c: Tangent(g5,g6) = 1.5708
    c: Coincident(g6,g7)
    c: Vertical(g7)
    c: Coincident(g7,g8)
    c: Coincident(g8,g4)
    c: Horizontal(g8)
    c: Vertical(g4)
    c: Horizontal(g6)
    c: Coincident(g4,g-1)
    c: Radius(g5) = 5
    c: DistanceY(g5,g4) = 35
    c: DistanceX(g6,g6) = 30
FEATURE [PartDesign::Pad] Pad
  Direction = (1,1,1)
  Length = 1
  Length2 = 30
  Placement = pos=(0,0,0) rot=(1,0,0;1.5708rad)
  Profile = -> Sketch
  Reversed = true
  Type = 4
FEATURE [Sketcher::SketchObject] Sketch001
  FullyConstrained = true
  MapMode = 5
  Placement = pos=(0,0,0) rot=(0.57735,0.57735,0.57735;2.0944rad)
  Support = -> [YZ_Plane]
  sketch-geometry (6):
    g0: LineSegment StartX=0 StartY=0 StartZ=0 EndX=0 EndY=-15 EndZ=0
    g1: ArcOfCircle CenterX=5 CenterY=-15 CenterZ=0 NormalX=0 NormalY=0 NormalZ=1 AngleXU=0 Radius=5 StartAngle=3.14159 EndAngle=4.1047
    g2: LineSegment StartX=2.14515 StartY=-19.1049 StartZ=0 EndX=25 EndY=-35 EndZ=0
    g3: LineSegment StartX=25 StartY=-35 StartZ=0 EndX=100 EndY=-35 EndZ=0
    g4: LineSegment StartX=100 StartY=-35 StartZ=0 EndX=100 EndY=0 EndZ=0
    g5: LineSegment StartX=100 StartY=0 StartZ=0 EndX=0 EndY=0 EndZ=0
  constraints (16):
    c: Vertical(g0)
    c: Tangent(g0,g1) = -1.5708
    c: Tangent(g1,g2) = -1.5708
    c: Coincident(g2,g3)
    c: Horizontal(g3)
    c: Coincident(g3,g4)
    c: Vertical(g4)
    c: Coincident(g4,g5)
    c: Coincident(g5,g0)
    c: Horizontal(g5)
    c: Radius(g1) = 5
    c: Coincident(g0,g-1)
    c: DistanceY(g4,g4) = 35
    c: DistanceX(g5,g5) = 100
    c: DistanceX(g0,g2) = 25  'stepover'
    c: DistanceY(g0,g0) = 15
FEATURE [PartDesign::Pocket] Pocket
  BaseFeature = -> Pad
  Length = 5
  Length2 = 100
  Midplane = true
  Placement = pos=(0,0,0) rot=(1,0,0;1.5708rad)
  Profile = -> Sketch001
  Type = 1
FEATURE [PartDesign::Body] Body  label="tube1_guideblock"
  Group = -> [Sketch,Pad,Sketch001,Pocket]
  Origin = -> Origin
  Tip = -> Pocket
FEATURE [Sketcher::SketchObject] Sketch003
  FullyConstrained = true
  MapMode = 5
  Support = -> [XY_Plane001]
  expr: Constraints[2] = 0.1in
  expr: Constraints[3] = 0.156in
  sketch-geometry (2):
    g0: Circle CenterX=0 CenterY=0 CenterZ=0 NormalX=0 NormalY=0 NormalZ=1 AngleXU=0 Radius=1.27
    g1: Circle CenterX=0 CenterY=0 CenterZ=0 NormalX=0 NormalY=0 NormalZ=1 AngleXU=0 Radius=1.9812
  constraints (4):
    c: Coincident(g0,g-1)
    c: Coincident(g1,g0)
    c: Diameter(g0) = 2.54
    c: Diameter(g1) = 3.9624
FEATURE [Sketcher::SketchObject] Sketch004
  FullyConstrained = true
  MapMode = 5
  Placement = pos=(0,0,0) rot=(1,0,0;1.5708rad)
  Support = -> [XZ_Plane002]
  sketch-geometry (6):
    g0: LineSegment StartX=0 StartY=0 StartZ=0 EndX=40 EndY=0 EndZ=0
    g1: LineSegment StartX=40 StartY=0 StartZ=0 EndX=40 EndY=10 EndZ=0
    g2: LineSegment StartX=40 StartY=10 StartZ=0 EndX=0 EndY=10 EndZ=0
    g3: LineSegment StartX=0 StartY=10 StartZ=0 EndX=0 EndY=0 EndZ=0
    g4: Circle CenterX=4.5 CenterY=5 CenterZ=0 NormalX=0 NormalY=0 NormalZ=1 AngleXU=0 Radius=1.75
    g5: Circle CenterX=16.5 CenterY=5 CenterZ=0 NormalX=0 NormalY=0 NormalZ=1 AngleXU=0 Radius=1.75
  constraints (17):
    c: Coincident(g0,g1)
    c: Coincident(g1,g2)
    c: Coincident(g2,g3)
    c: Coincident(g3,g0)
    c: Horizontal(g0)
    c: Horizontal(g2)
    c: Vertical(g1)
    c: Vertical(g3)
    c: Coincident(g0,g-1)
    c: DistanceY(g3,g3) = 10
    c: DistanceX(g2,g2) = 40
    c: Horizontal(g5,g4)
    c: DistanceX(g4,g5) = 12
    c: DistanceY(g0,g4) = 5
    c: DistanceX(g0,g4) = 4.5
    c: Equal(g5,g4)
    c: Diameter(g5) = 3.5
FEATURE [PartDesign::Pad] Pad001
  Direction = (1,1,1)
  Length = 1
  Length2 = 100
  Placement = pos=(0,0,0) rot=(1,0,0;1.5708rad)
  Profile = -> Sketch004
  Type = 0
FEATURE [PartDesign::Body] Body002  label="plate"
  Group = -> [Sketch004,Pad001]
  Origin = -> Origin002
  Placement = pos=(-37,-2,-10) rot=(0,0,1;0rad)
  Tip = -> Pad001
FEATURE [PartDesign::SubShapeBinder] Binder
  BindMode = 0
  ClaimChildren = false
  Context = -> <external watercooled_print_head.FCStd>#Model [part_cooling_duct_part_cooling_duct.Body001.Binder.]
  Fuse = false
  MakeFace = true
  PartialLoad = false
  Relative = true
  Support = -> [Body[Pocket.Edge1,Pocket.Edge2,Pocket.Edge3,Pocket.Edge12,Pocket.Edge13]]
  _Version = 2
FEATURE [Sketcher::SketchObject] Sketch005
  FullyConstrained = true
  MapMode = 5
  Placement = pos=(0,0,0) rot=(0.57735,0.57735,0.57735;2.0944rad)
  Support = -> [YZ_Plane005]
  sketch-geometry (6):
    g0: LineSegment StartX=0 StartY=0 StartZ=0 EndX=0 EndY=-15 EndZ=0
    g1: ArcOfCircle CenterX=5 CenterY=-15 CenterZ=0 NormalX=0 NormalY=0 NormalZ=1 AngleXU=0 Radius=5 StartAngle=3.14159 EndAngle=3.44391
    g2: LineSegment StartX=0.226753 StartY=-16.4887 StartZ=0 EndX=6 EndY=-35 EndZ=0
    g3: LineSegment StartX=6 StartY=-35 StartZ=0 EndX=100 EndY=-35 EndZ=0
    g4: LineSegment StartX=100 StartY=-35 StartZ=0 EndX=100 EndY=0 EndZ=0
    g5: LineSegment StartX=100 StartY=0 StartZ=0 EndX=0 EndY=0 EndZ=0
  constraints (16):
    c: Vertical(g0)
    c: Tangent(g0,g1) = -1.5708
    c: Tangent(g1,g2) = -1.5708
    c: Coincident(g2,g3)
    c: Horizontal(g3)
    c: Coincident(g3,g4)
    c: Vertical(g4)
    c: Coincident(g4,g5)
    c: Coincident(g5,g0)
    c: Horizontal(g5)
    c: Radius(g1) = 5
    c: Coincident(g0,g-1)
    c: DistanceY(g4,g4) = 35
    c: DistanceX(g5,g5) = 100
    c: DistanceX(g0,g2) = 6  'stepover'
    c: DistanceY(g0,g0) = 15
FEATURE [Sketcher::SketchObject] Sketch006
  FullyConstrained = true
  MapMode = 5
  Placement = pos=(0,0,0) rot=(1,0,0;1.5708rad)
  Support = -> [XZ_Plane004]
  sketch-geometry (9):
    g0: LineSegment StartX=0 StartY=0 StartZ=0 EndX=-50 EndY=0 EndZ=0
    g1: LineSegment StartX=-50 StartY=0 StartZ=0 EndX=-50 EndY=15 EndZ=0
    g2: LineSegment StartX=-50 StartY=15 StartZ=0 EndX=0 EndY=15 EndZ=0
    g3: LineSegment StartX=0 StartY=15 StartZ=0 EndX=0 EndY=0 EndZ=0
    g4: LineSegment StartX=0 StartY=0 StartZ=0 EndX=0 EndY=-30 EndZ=0
    g5: ArcOfCircle CenterX=-5 CenterY=-30 CenterZ=0 NormalX=0 NormalY=0 NormalZ=1 AngleXU=0 Radius=5 StartAngle=4.71239 EndAngle=6.28319
    g6: LineSegment StartX=-5 StartY=-35 StartZ=0 EndX=-30 EndY=-35 EndZ=0
    g7: LineSegment StartX=-30 StartY=-35 StartZ=0 EndX=-30 EndY=0 EndZ=0
    g8: LineSegment StartX=-30 StartY=0 StartZ=0 EndX=0 EndY=0 EndZ=0
  constraints (24):
    c: Coincident(g0,g1)
    c: Coincident(g1,g2)
    c: Coincident(g2,g3)
    c: Coincident(g3,g0)
    c: Horizontal(g0)
    c: Horizontal(g2)
    c: Vertical(g1)
    c: Vertical(g3)
    c: Coincident(g0,g-1)
    c: DistanceX(g2,g2) = 50
    c: DistanceY(g1,g1) = 15
    c: Tangent(g4,g5) = 1.5708
    c: Tangent(g5,g6) = 1.5708
    c: Coincident(g6,g7)
    c: Vertical(g7)
    c: Coincident(g7,g8)
    c: Coincident(g8,g4)
    c: Horizontal(g8)
    c: Vertical(g4)
    c: Horizontal(g6)
    c: Coincident(g4,g-1)
    c: Radius(g5) = 5
    c: DistanceY(g5,g4) = 35
    c: DistanceX(g6,g6) = 25
FEATURE [PartDesign::Pad] Pad002
  Direction = (1,1,1)
  Length = 1
  Length2 = 30
  Placement = pos=(0,0,0) rot=(1,0,0;1.5708rad)
  Profile = -> Sketch006
  Reversed = true
  Type = 4
FEATURE [PartDesign::Pocket] Pocket001
  BaseFeature = -> Pad002
  Length = 5
  Length2 = 100
  Midplane = true
  Placement = pos=(0,0,0) rot=(1,0,0;1.5708rad)
  Profile = -> Sketch005
  Type = 1
FEATURE [PartDesign::Body] Body004  label="tube2_guideblock"
  Group = -> [Sketch006,Pad002,Sketch005,Pocket001]
  Origin = -> Origin004
  Placement = pos=(-5,0,0) rot=(0,0,1;0rad)
  Tip = -> Pocket001
FEATURE [Sketcher::SketchObject] Sketch007
  FullyConstrained = true
  MapMode = 5
  Support = -> [XY_Plane005]
  expr: Constraints[3] = 0.156in
  expr: Constraints[2] = 0.1in
  sketch-geometry (2):
    g0: Circle CenterX=0 CenterY=0 CenterZ=0 NormalX=0 NormalY=0 NormalZ=1 AngleXU=0 Radius=1.27
    g1: Circle CenterX=0 CenterY=0 CenterZ=0 NormalX=0 NormalY=0 NormalZ=1 AngleXU=0 Radius=1.9812
  constraints (4):
    c: Coincident(g0,g-1)
    c: Coincident(g1,g0)
    c: Diameter(g0) = 2.54
    c: Diameter(g1) = 3.9624
FEATURE [PartDesign::SubShapeBinder] Binder001
  BindMode = 0
  ClaimChildren = false
  Context = -> <external watercooled_print_head.FCStd>#Model [part_cooling_duct_part_cooling_duct.Body003.Binder001.]
  Fuse = false
  MakeFace = true
  PartialLoad = false
  Relative = true
  Support = -> [Body004[Pocket001.Edge1,Pocket001.Edge2,Pocket001.Edge3,Pocket001.Edge12,Pocket001.Edge13]]
  _Version = 2
FEATURE [PartDesign::AdditivePipe] AdditivePipe
  AuxilleryCurvelinear = true
  AuxillerySpineTangent = false
  Binormal = (0,0,0)
  Mode = 0
  Profile = -> Sketch003
  Spine = -> Binder
  SpineTangent = false
  Transformation = 0
  Transition = 0
FEATURE [PartDesign::Body] Body001  label="tube1"
  Group = -> [Sketch003,Binder,AdditivePipe]
  Origin = -> Origin001
  Tip = -> AdditivePipe
FEATURE [PartDesign::AdditivePipe] AdditivePipe001
  AuxilleryCurvelinear = true
  AuxillerySpineTangent = false
  Binormal = (0,0,0)
  Mode = 0
  Profile = -> Sketch007
  Spine = -> Binder001
  SpineTangent = false
  Transformation = 0
  Transition = 0
FEATURE [PartDesign::Body] Body003  label="tube2"
  Group = -> [Sketch007,Binder001,AdditivePipe001]
  Origin = -> Origin005
  Placement = pos=(-5,0,0) rot=(0,0,1;0rad)
  Tip = -> AdditivePipe001
FEATURE [App::Part] Part  label="part_cooling_duct"
  Group = -> [Body,Body001,Body002,Body003,Body004]
  Origin = -> Origin003
---- part silicone_tube.FCStd = doc fcstd_1b31c093d3db ----
FCSTD DOCUMENT  (FreeCAD 0.19R24267 (Git))
Label: silicone_tube
License: All rights reserved
LicenseURL: http://en.wikipedia.org/wiki/All_rights_reserved
objects: Sketcher::SketchObject×2, PartDesign::AdditivePipe×1, PartDesign::Body×1, PartDesign::CoordinateSystem×1, App::Part×1
note: 6 computed .brp shape members not serialized (recipe doc carries the construction recipe); baked Part::Feature solids carry a one-line shape summary decoded from their .brp

FEATURE [Sketcher::SketchObject] Sketch085
  FullyConstrained = false
  MapMode = 5
  Placement = pos=(0,0,0) rot=(0.57735,0.57735,0.57735;2.0944rad)
  Support = -> [YZ_Plane099]
  sketch-geometry (4):
    g0: LineSegment StartX=0 StartY=0 StartZ=0 EndX=8.08004 EndY=0 EndZ=0
    g1: ArcOfCircle CenterX=8.08004 CenterY=7.47139 CenterZ=0 NormalX=0 NormalY=0 NormalZ=1 AngleXU=0 Radius=7.47139 StartAngle=4.71239 EndAngle=7.5108
    g2: ArcOfCircle CenterX=16.5072 CenterY=31.0557 CenterZ=0 NormalX=0 NormalY=0 NormalZ=1 AngleXU=0 Radius=17.5733 StartAngle=3.14159 EndAngle=4.36921
    g3: LineSegment StartX=-1.06608 StartY=31.0557 StartZ=0 EndX=-1.06608 EndY=57.8085 EndZ=0
  constraints (6):
    c: Coincident(g0,g-1)
    c: Horizontal(g0)
    c: Tangent(g3,g2) = 1.5708
    c: Tangent(g2,g1) = 1.5708
    c: Tangent(g1,g0) = -1.5708
    c: Vertical(g3)
FEATURE [Sketcher::SketchObject] Sketch086
  FullyConstrained = false
  MapMode = 5
  Placement = pos=(0,0,0) rot=(1,0,0;1.5708rad)
  Support = -> [XZ_Plane099]
  sketch-geometry (2):
    g0: Circle CenterX=0 CenterY=0 CenterZ=0 NormalX=0 NormalY=0 NormalZ=1 AngleXU=0 Radius=2
    g1: Circle CenterX=0 CenterY=0 CenterZ=0 NormalX=0 NormalY=0 NormalZ=1 AngleXU=0 Radius=3
  constraints (4):
    c: Coincident(g0,g-1)
    c: Coincident(g1,g0)
    c: Diameter(g1) = 6
    c: Diameter(g0) = 4
FEATURE [PartDesign::AdditivePipe] AdditivePipe002
  AuxilleryCurvelinear = true
  AuxillerySpineTangent = false
  Binormal = (0,0,0)
  Mode = 2
  Placement = pos=(0,0,0) rot=(1,0,0;1.5708rad)
  Profile = -> Sketch086
  Spine = -> Sketch085
  SpineTangent = false
  Transformation = 0
  Transition = 0
FEATURE [PartDesign::Body] Body032  label="Body"
  Group = -> [Sketch085,Sketch086,AdditivePipe002]
  Origin = -> Origin099
  Tip = -> AdditivePipe002
FEATURE [PartDesign::CoordinateSystem] LCS_1
  AttacherType = Attacher::AttachEngine3D
  MapMode = 11
  Placement = pos=(0,0,0) rot=(0.57735,-0.57735,0.57735;2.0944rad)
  Support = -> [AdditivePipe002]
FEATURE [App::Part] Part  label="silicone_tube"
  Group = -> [Body032,LCS_1]
  Origin = -> Origin
---- part watercooled_block.FCStd = doc fcstd_938d0ff1167d ----
FCSTD DOCUMENT  (FreeCAD 0.19R24267 (Git))
Label: watercooled_block
License: All rights reserved
LicenseURL: http://en.wikipedia.org/wiki/All_rights_reserved
objects: TechDraw::DrawViewDimension×38, Sketcher::SketchObject×11, PartDesign::CoordinateSystem×10, TechDraw::DrawViewAnnotation×9, TechDraw::DrawLeaderLine×9, PartDesign::Hole×8, TechDraw::DrawProjGroupItem×6, PartDesign::Pad×2, PartDesign::Pocket×1, PartDesign::Fillet×1, PartDesign::Chamfer×1, PartDesign::Body×1, TechDraw::DrawSVGTemplate×1, TechDraw::DrawViewPart×1, TechDraw::DrawProjGroup×1, TechDraw::DrawPage×1, App::Part×1
note: 48 computed .brp shape members not serialized (recipe doc carries the construction recipe); baked Part::Feature solids carry a one-line shape summary decoded from their .brp

FEATURE [Sketcher::SketchObject] Sketch051
  FullyConstrained = false
  MapMode = 5
  Placement = pos=(0,0,0) rot=(1,0,0;1.5708rad)
  Support = -> [XZ_Plane061]
  sketch-geometry (10):
    g0: LineSegment StartX=18 StartY=0 StartZ=0 EndX=18 EndY=11 EndZ=0
    g1: LineSegment StartX=18 StartY=11 StartZ=0 EndX=-12 EndY=11 EndZ=0
    g2: LineSegment StartX=-18.35 StartY=0 StartZ=0 EndX=-18.35 EndY=50 EndZ=0
    g3: LineSegment StartX=-18.35 StartY=50 StartZ=0 EndX=-12 EndY=50 EndZ=0
    g4: LineSegment StartX=-12 StartY=50 StartZ=0 EndX=-12 EndY=28.75 EndZ=0
    g5: LineSegment StartX=-18.35 StartY=0 StartZ=0 EndX=18 EndY=0 EndZ=0
    g6: LineSegment StartX=-12 StartY=28.75 StartZ=0 EndX=-14 EndY=28.75 EndZ=0
    g7: LineSegment StartX=-14 StartY=28.75 StartZ=0 EndX=-14 EndY=21.25 EndZ=0
    g8: LineSegment StartX=-14 StartY=21.25 StartZ=0 EndX=-12 EndY=21.25 EndZ=0
    g9: LineSegment StartX=-12 StartY=21.25 StartZ=0 EndX=-12 EndY=11 EndZ=0
  constraints (29):
    c: Coincident(g0,g1)
    c: Horizontal(g1)
    c: Vertical(g0)
    c: Coincident(g2,g3)
    c: Coincident(g3,g4)
    c: Horizontal(g3)
    c: Vertical(g2)
    c: Vertical(g4)
    c: DistanceX(g3,g3) = 6.35
    c: DistanceX(g1,g-1) = 12
    c: Coincident(g1,g9)
    c: DistanceY(g0,g0) = 11
    c: DistanceY(g2,g2) = 50
    c: DistanceX(g-1,g0) = 18
    c: Coincident(g5,g2)
    c: Coincident(g5,g0)
    c: Horizontal(g5)
    c: PointOnObject(g-1,g5)
    c: Horizontal(g6)
    c: Coincident(g7,g6)
    c: Vertical(g7)
    c: Coincident(g8,g7)
    c: Horizontal(g8)
    c: Coincident(g4,g6)
    c: Coincident(g9,g8)
    c: Tangent(g4,g9)
    c: DistanceY(g7,g7) = 7.5
    c: DistanceY(g-1,g8) = 21.25
    c: DistanceX(g6,g6) = 2
FEATURE [PartDesign::Pad] Pad021  label="Pad022"
  AllowMultiFace = false
  Direction = (1,1,1)
  Length = 50
  Length2 = 100
  Midplane = true
  Placement = pos=(0,0,0) rot=(1,0,0;1.5708rad)
  Profile = -> Sketch051
  Type = 0
FEATURE [Sketcher::SketchObject] Sketch052
  AttachmentOffset = pos=(0,0,12) rot=(0,0,1;0rad)
  FullyConstrained = false
  MapMode = 5
  Placement = pos=(0,12,2.7e-15) rot=(0,0.707107,0.707107;3.14159rad)
  Support = -> [XZ_Plane061]
  sketch-geometry (3):
    g0: Circle CenterX=-6.35 CenterY=5.5 CenterZ=0 NormalX=0 NormalY=0 NormalZ=1 AngleXU=0 Radius=3.175
    g1: Circle CenterX=6.35 CenterY=5.5 CenterZ=0 NormalX=0 NormalY=0 NormalZ=1 AngleXU=0 Radius=3.175
    g2: LineSegment StartX=-6.35 StartY=5.5 StartZ=0 EndX=6.35 EndY=5.5 EndZ=0
  constraints (8):
    c: Diameter(g0) = 6.35
    c: Diameter(g1) = 6.35
    c: DistanceY(g-1,g0) = 5.5
    c: Coincident(g2,g0)
    c: Coincident(g2,g1)
    c: Horizontal(g2)
    c: DistanceX(g2,g2) = 12.7
    c: DistanceX(g0,g-1) = 6.35
FEATURE [Sketcher::SketchObject] Sketch053
  AttachmentOffset = pos=(0,0,18.35) rot=(0,0,1;0rad)
  FullyConstrained = false
  MapMode = 5
  Placement = pos=(-18.35,4.1e-15,-4.1e-15) rot=(-0.57735,0.57735,0.57735;4.18879rad)
  Support = -> [YZ_Plane061]
  sketch-geometry (1):
    g0: Circle CenterX=16 CenterY=5.5 CenterZ=0 NormalX=0 NormalY=0 NormalZ=1 AngleXU=0 Radius=2.5
  constraints (3):
    c: Diameter(g0) = 5
    c: DistanceY(g-1,g0) = 5.5
    c: DistanceX(g-1,g0) = 16
FEATURE [PartDesign::Hole] Hole006
  AllowMultiFace = false
  BaseFeature = -> Pad021
  Depth = 27
  DepthType = 0
  Diameter = 4.763
  DrillForDepth = false
  DrillPoint = 1
  DrillPointAngle = 118
  HoleCutCountersinkAngle = 90
  HoleCutCustomValues = false
  HoleCutDepth = 11
  HoleCutDiameter = 6
  HoleCutType = 1
  ModelActualThread = false
  Placement = pos=(0,0,0) rot=(1,0,0;1.5708rad)
  Profile = -> Sketch053
  Tapered = false
  TaperedAngle = 90
  ThreadAngle = 0
  ThreadClass = 0
  ThreadCutOffInner = 0
  ThreadCutOffOuter = 0
  ThreadDirection = 0
  ThreadFit = 0
  ThreadPitch = 0
  ThreadSize = 0
  ThreadType = 0
  Threaded = false
FEATURE [Sketcher::SketchObject] Sketch054
  FullyConstrained = false
  MapMode = 5
  Placement = pos=(0,0,0) rot=(0,1,0;3.14159rad)
  Support = -> [XY_Plane061]
  sketch-geometry (1):
    g0: Circle CenterX=0 CenterY=-6 CenterZ=0 NormalX=0 NormalY=0 NormalZ=1 AngleXU=0 Radius=2
  constraints (3):
    c: Diameter(g0) = 4
    c: PointOnObject(g0,g-2)
    c: DistanceY(g0,g-1) = 6
FEATURE [PartDesign::Hole] Hole007
  AllowMultiFace = false
  BaseFeature = -> Hole006
  Depth = 25
  DepthType = 1
  Diameter = 4
  DrillForDepth = false
  DrillPoint = 1
  DrillPointAngle = 118
  HoleCutCountersinkAngle = 90
  HoleCutCustomValues = false
  HoleCutDepth = 0
  HoleCutDiameter = 0
  HoleCutType = 0
  ModelActualThread = false
  Placement = pos=(0,0,0) rot=(1,0,0;1.5708rad)
  Profile = -> Sketch054
  Tapered = false
  TaperedAngle = 90
  ThreadAngle = 0
  ThreadClass = 0
  ThreadCutOffInner = 0
  ThreadCutOffOuter = 0
  ThreadDirection = 0
  ThreadFit = 0
  ThreadPitch = 0
  ThreadSize = 0
  ThreadType = 0
  Threaded = false
FEATURE [Sketcher::SketchObject] Sketch055
  AttachmentOffset = pos=(0,0,-12) rot=(0,0,1;0rad)
  FullyConstrained = false
  MapMode = 5
  Placement = pos=(-12,2.7e-15,-2.7e-15) rot=(0.57735,0.57735,0.57735;2.0944rad)
  Support = -> [YZ_Plane061]
  expr: Constraints[3] = 25 + 31.9 / 2
  sketch-geometry (2):
    g0: Circle CenterX=-15 CenterY=40.95 CenterZ=0 NormalX=0 NormalY=0 NormalZ=1 AngleXU=0 Radius=2.55
    g1: Circle CenterX=15 CenterY=40.95 CenterZ=0 NormalX=0 NormalY=0 NormalZ=1 AngleXU=0 Radius=2.55
  constraints (5):
    c: Diameter(g1) = 5.1
    c: Equal(g1,g0)
    c: DistanceX(g0,g1) = 30
    c: DistanceY(g-1,g0) = 40.95
    c: Symmetric(g0,g1,g-2)
FEATURE [PartDesign::Hole] Hole008
  AllowMultiFace = false
  BaseFeature = -> Hole007
  Depth = 25
  DepthType = 1
  Diameter = 7.14
  DrillForDepth = false
  DrillPoint = 1
  DrillPointAngle = 118
  HoleCutCountersinkAngle = 90
  HoleCutCustomValues = false
  HoleCutDepth = 2.17
  HoleCutDiameter = 12
  HoleCutType = 1
  ModelActualThread = false
  Placement = pos=(0,0,0) rot=(1,0,0;1.5708rad)
  Profile = -> Sketch055
  Tapered = false
  TaperedAngle = 90
  ThreadAngle = 0
  ThreadClass = 0
  ThreadCutOffInner = 0
  ThreadCutOffOuter = 0
  ThreadDirection = 0
  ThreadFit = 0
  ThreadPitch = 0
  ThreadSize = 0
  ThreadType = 0
  Threaded = false
  expr: HoleCutDepth = 6.35 - 4.18
FEATURE [Sketcher::SketchObject] Sketch056
  AttachmentOffset = pos=(0,0,18.35) rot=(0,0,1;0rad)
  FullyConstrained = false
  MapMode = 5
  Placement = pos=(-18.35,4.1e-15,-4.1e-15) rot=(-0.57735,0.57735,0.57735;4.18879rad)
  Support = -> [YZ_Plane061]
  expr: Constraints[2] = 25 - 31.9 / 2
  sketch-geometry (1):
    g0: Circle CenterX=0 CenterY=9.05 CenterZ=0 NormalX=0 NormalY=0 NormalZ=1 AngleXU=0 Radius=2.5
  constraints (3):
    c: PointOnObject(g0,g-2)
    c: Diameter(g0) = 5
    c: DistanceY(g-1,g0) = 9.05
FEATURE [Sketcher::SketchObject] Sketch057
  AttachmentOffset = pos=(0,0,11) rot=(0,0,1;0rad)
  FullyConstrained = false
  MapMode = 5
  Placement = pos=(0,0,11) rot=(0,0,1;0rad)
  Support = -> [XY_Plane061]
  sketch-geometry (4):
    g0: LineSegment StartX=23 StartY=32 StartZ=0 EndX=-12 EndY=32 EndZ=0
    g1: LineSegment StartX=-12 StartY=32 StartZ=0 EndX=-12 EndY=12 EndZ=0
    g2: LineSegment StartX=-12 StartY=12 StartZ=0 EndX=23 EndY=12 EndZ=0
    g3: LineSegment StartX=23 StartY=12 StartZ=0 EndX=23 EndY=32 EndZ=0
  constraints (12):
    c: Coincident(g0,g1)
    c: Coincident(g1,g2)
    c: Coincident(g2,g3)
    c: Coincident(g3,g0)
    c: Horizontal(g0)
    c: Horizontal(g2)
    c: Vertical(g1)
    c: Vertical(g3)
    c: DistanceX(g1,g-1) = 12
    c: DistanceX(g2,g2) = 35
    c: DistanceY(g3,g3) = 20
    c: DistanceY(g-1,g2) = 12
FEATURE [PartDesign::Pocket] Pocket019
  AllowMultiFace = false
  BaseFeature = -> Hole008
  Length = 5
  Length2 = 100
  Placement = pos=(0,0,0) rot=(1,0,0;1.5708rad)
  Profile = -> Sketch057
  Type = 1
FEATURE [PartDesign::Hole] Hole009
  AllowMultiFace = false
  BaseFeature = -> Pocket019
  Depth = 32
  DepthType = 0
  Diameter = 4.7625
  DrillForDepth = false
  DrillPoint = 1
  DrillPointAngle = 118
  HoleCutCountersinkAngle = 90
  HoleCutCustomValues = false
  HoleCutDepth = 7.3
  HoleCutDiameter = 6
  HoleCutType = 1
  ModelActualThread = false
  Placement = pos=(0,0,0) rot=(1,0,0;1.5708rad)
  Profile = -> Sketch052
  Tapered = false
  TaperedAngle = 90
  ThreadAngle = 0
  ThreadClass = 0
  ThreadCutOffInner = 0
  ThreadCutOffOuter = 0
  ThreadDirection = 0
  ThreadFit = 0
  ThreadPitch = 0
  ThreadSize = 0
  ThreadType = 0
  Threaded = false
  expr: Diameter = 3 / 16 * 25.4
FEATURE [Sketcher::SketchObject] Sketch058
  AttachmentOffset = pos=(0,0,11) rot=(0,0,1;0rad)
  FullyConstrained = false
  MapMode = 5
  Placement = pos=(0,0,11) rot=(0,0,1;0rad)
  Support = -> [XY_Plane061]
  sketch-geometry (12):
    g0: LineSegment StartX=13 StartY=-14.75 StartZ=0 EndX=13 EndY=3.25 EndZ=0
    g1: LineSegment StartX=10.75 StartY=5.5 StartZ=0 EndX=-3.75 EndY=5.5 EndZ=0
    g2: LineSegment StartX=-6 StartY=3.25 StartZ=0 EndX=-6 EndY=-14.75 EndZ=0
    g3: LineSegment StartX=-3.75 StartY=-17 StartZ=0 EndX=10.75 EndY=-17 EndZ=0
    g4: LineSegment StartX=18 StartY=-25 StartZ=0 EndX=-12 EndY=-25 EndZ=0
    g5: LineSegment StartX=-12 StartY=-25 StartZ=0 EndX=-12 EndY=12 EndZ=0
    g6: LineSegment StartX=-12 StartY=12 StartZ=0 EndX=18 EndY=12 EndZ=0
    g7: LineSegment StartX=18 StartY=12 StartZ=0 EndX=18 EndY=-25 EndZ=0
    g8: ArcOfCircle CenterX=10.75 CenterY=3.25 CenterZ=0 NormalX=0 NormalY=0 NormalZ=1 AngleXU=0 Radius=2.25 StartAngle=3.758e-13 EndAngle=1.5708
    g9: ArcOfCircle CenterX=-3.75 CenterY=3.25 CenterZ=0 NormalX=0 NormalY=0 NormalZ=1 AngleXU=0 Radius=2.25 StartAngle=1.5708 EndAngle=3.14159
    g10: ArcOfCircle CenterX=-3.75 CenterY=-14.75 CenterZ=0 NormalX=0 NormalY=0 NormalZ=1 AngleXU=0 Radius=2.25 StartAngle=3.14159 EndAngle=4.71239
    g11: ArcOfCircle CenterX=10.75 CenterY=-14.75 CenterZ=0 NormalX=0 NormalY=0 NormalZ=1 AngleXU=0 Radius=2.25 StartAngle=4.71239 EndAngle=6.28319
  constraints (32):
    c: Vertical(g0)
    c: Horizontal(g1)
    c: Vertical(g2)
    c: Horizontal(g3)
    c: Horizontal(g4)
    c: Coincident(g4,g5)
    c: Vertical(g5)
    c: Coincident(g5,g6)
    c: Horizontal(g6)
    c: Coincident(g6,g7)
    c: Vertical(g7)
    c: Tangent(g1,g8) = -1.5708
    c: Tangent(g0,g8) = -1.5708
    c: Tangent(g1,g9) = -1.5708
    c: Tangent(g2,g9) = -1.5708
    c: Tangent(g3,g10) = -1.5708
    c: Tangent(g2,g10) = -1.5708
    c: DistanceY(g-1,g6) = 12
    c: DistanceY(g4,g-1) = 25
    c: DistanceY(g-1,g1) = 5.5
    c: DistanceX(g2,g-1) = 6
    c: DistanceX(g-1,g0) = 13
    c: DistanceX(g-1,g6) = 18
    c: Equal(g9,g8)
    c: Diameter(g10) = 4.5
    c: DistanceX(g5,g-1) = 12
    c: Coincident(g7,g4)
    c: Tangent(g0,g11) = -1.5708
    c: Tangent(g3,g11) = -1.5708
    c: Equal(g10,g11)
    c: DistanceY(g3,g-1) = 17
    c: Equal(g10,g9)
FEATURE [PartDesign::Pad] Pad022  label="Pad023"
  AllowMultiFace = false
  BaseFeature = -> Hole009
  Direction = (1,1,1)
  Length = 4
  Length2 = 100
  Placement = pos=(0,0,0) rot=(1,0,0;1.5708rad)
  Profile = -> Sketch058
  Type = 0
FEATURE [Sketcher::SketchObject] Sketch059
  AttachmentOffset = pos=(0,0,15) rot=(0,0,1;0rad)
  FullyConstrained = false
  MapMode = 5
  Placement = pos=(0,0,15) rot=(0,0,1;0rad)
  Support = -> [XY_Plane061]
  sketch-geometry (3):
    g0: Circle CenterX=15.5 CenterY=-3.95 CenterZ=0 NormalX=0 NormalY=0 NormalZ=1 AngleXU=0 Radius=1.5
    g1: Circle CenterX=5.25 CenterY=7.85 CenterZ=0 NormalX=0 NormalY=0 NormalZ=1 AngleXU=0 Radius=1.5
    g2: Circle CenterX=-4.75 CenterY=-20.25 CenterZ=0 NormalX=0 NormalY=0 NormalZ=1 AngleXU=0 Radius=1.5
  constraints (9):
    c: DistanceY(g2,g-1) = 20.25
    c: DistanceX(g2,g-1) = 4.75
    c: DistanceX(g-1,g0) = 15.5
    c: DistanceX(g-1,g1) = 5.25
    c: DistanceY(g-1,g1) = 7.85
    c: DistanceY(g0,g-1) = 3.95
    c: Equal(g1,g0)
    c: Equal(g0,g2)
    c: Diameter(g1) = 3
FEATURE [PartDesign::Hole] Hole010
  AllowMultiFace = false
  BaseFeature = -> Pad022
  Depth = 6
  DepthType = 0
  Diameter = 1.4
  DrillForDepth = false
  DrillPoint = 1
  DrillPointAngle = 118
  HoleCutCountersinkAngle = 90
  HoleCutCustomValues = false
  HoleCutDepth = 0
  HoleCutDiameter = 2.5
  HoleCutType = 0
  ModelActualThread = false
  Placement = pos=(0,0,0) rot=(1,0,0;1.5708rad)
  Profile = -> Sketch059
  Tapered = false
  TaperedAngle = 90
  ThreadAngle = 0
  ThreadClass = 0
  ThreadCutOffInner = 0
  ThreadCutOffOuter = 0
  ThreadDirection = 0
  ThreadFit = 0
  ThreadPitch = 0
  ThreadSize = 2
  ThreadType = 1
  Threaded = false
FEATURE [PartDesign::Hole] Hole011
  AllowMultiFace = false
  BaseFeature = -> Hole010
  Depth = 10
  DepthType = 0
  Diameter = 1.6
  DrillForDepth = false
  DrillPoint = 1
  DrillPointAngle = 118
  HoleCutCountersinkAngle = 90
  HoleCutCustomValues = false
  HoleCutDepth = 0
  HoleCutDiameter = 5
  HoleCutType = 0
  ModelActualThread = false
  Placement = pos=(0,0,0) rot=(1,0,0;1.5708rad)
  Profile = -> Sketch056
  Tapered = false
  TaperedAngle = 90
  ThreadAngle = 60
  ThreadClass = 0
  ThreadCutOffInner = 0.0433013
  ThreadCutOffOuter = 0.0866025
  ThreadDirection = 1
  ThreadFit = 0
  ThreadPitch = 0.4
  ThreadSize = 6
  ThreadType = 1
  Threaded = true
FEATURE [Sketcher::SketchObject] Sketch060
  FullyConstrained = false
  MapMode = 5
  Placement = pos=(0,0,0) rot=(0.57735,0.57735,0.57735;2.0944rad)
  Support = -> [YZ_Plane061]
  sketch-geometry (1):
    g0: Circle CenterX=0 CenterY=25 CenterZ=0 NormalX=0 NormalY=0 NormalZ=1 AngleXU=0 Radius=1.5
  constraints (3):
    c: PointOnObject(g0,g-2)
    c: DistanceY(g-1,g0) = 25
    c: Diameter(g0) = 3
FEATURE [PartDesign::Hole] Hole012
  AllowMultiFace = false
  BaseFeature = -> Hole011
  Depth = 25
  DepthType = 1
  Diameter = 1.6
  DrillForDepth = false
  DrillPoint = 1
  DrillPointAngle = 118
  HoleCutCountersinkAngle = 90
  HoleCutCustomValues = false
  HoleCutDepth = 0
  HoleCutDiameter = 3
  HoleCutType = 0
  ModelActualThread = false
  Placement = pos=(0,0,0) rot=(1,0,0;1.5708rad)
  Profile = -> Sketch060
  Tapered = false
  TaperedAngle = 90
  ThreadAngle = 0
  ThreadClass = 0
  ThreadCutOffInner = 0
  ThreadCutOffOuter = 0
  ThreadDirection = 0
  ThreadFit = 0
  ThreadPitch = 0
  ThreadSize = 3
  ThreadType = 1
  Threaded = false
FEATURE [PartDesign::Fillet] Fillet004
  Base = -> Hole012 [Edge9,Edge31,Edge57,Edge23,Edge19,Edge51,Edge1]
  BaseFeature = -> Hole012
  Placement = pos=(0,0,0) rot=(1,0,0;1.5708rad)
  Radius = 6.35
  SupportTransform = true
FEATURE [PartDesign::Chamfer] Chamfer002
  Angle = 45
  Base = -> Fillet004 [Edge25]
  BaseFeature = -> Fillet004
  ChamferType = 0
  FlipDirection = false
  Placement = pos=(0,0,0) rot=(1,0,0;1.5708rad)
  Size = 1.7
  Size2 = 1
  SupportTransform = true
FEATURE [Sketcher::SketchObject] Sketch073
  AttachmentOffset = pos=(0,0,18) rot=(0,0,1;0rad)
  FullyConstrained = false
  MapMode = 5
  Placement = pos=(18,-4e-15,4e-15) rot=(0.57735,0.57735,0.57735;2.0944rad)
  Support = -> [YZ_Plane061]
  sketch-geometry (2):
    g0: Circle CenterX=-0.5 CenterY=7 CenterZ=0 NormalX=0 NormalY=0 NormalZ=1 AngleXU=0 Radius=1.5
    g1: Circle CenterX=-12.5 CenterY=7 CenterZ=0 NormalX=0 NormalY=0 NormalZ=1 AngleXU=0 Radius=1.5
  constraints (6):
    c: Horizontal(g1,g0)
    c: Equal(g1,g0)
    c: Diameter(g0) = 3
    c: DistanceY(g-1,g0) = 7
    c: DistanceX(g1,g0) = 12
    c: DistanceX(g0,g-1) = 0.5
FEATURE [PartDesign::Hole] Hole014
  BaseFeature = -> Chamfer002
  Depth = 7
  DepthType = 0
  Diameter = 1.6
  DrillForDepth = false
  DrillPoint = 1
  DrillPointAngle = 118
  HoleCutCountersinkAngle = 90
  HoleCutCustomValues = false
  HoleCutDepth = 0
  HoleCutDiameter = 3
  HoleCutType = 0
  ModelActualThread = false
  Placement = pos=(0,0,0) rot=(1,0,0;1.5708rad)
  Profile = -> Sketch073
  Tapered = false
  TaperedAngle = 90
  ThreadAngle = 0
  ThreadClass = 0
  ThreadCutOffInner = 0
  ThreadCutOffOuter = 0
  ThreadDirection = 0
  ThreadFit = 0
  ThreadPitch = 0
  ThreadSize = 3
  ThreadType = 1
  Threaded = false
FEATURE [PartDesign::Body] Body021  label="block"
  Group = -> [Sketch051,Pad021,Sketch052,Sketch053,Hole006,Sketch054,Hole007,Sketch055,Hole008,Sketch056,Sketch057,Pocket019,Hole009,Sketch058,Pad022,Sketch059,Hole010,Hole011,Sketch060,Hole012,Fillet004,Chamfer002,Sketch073,Hole014]
  Origin = -> Origin061
  Tip = -> Hole014
FEATURE [TechDraw::DrawSVGTemplate] Template002
  EditableTexts = Author=Alex Neufeld; DWG_num=2020-105; Date=09/05/2020; Revision=1; Scale=NTS; Subtitle=For 20mm V-Slot Rail; Title=Watercooled Print Head
  Height = 215.9
  Orientation = 1
  Width = 279.4
FEATURE [TechDraw::DrawViewPart] View002
  CoarseView = false
  Direction = (0.577,-0.577,0.577)
  Focus = 100
  HardHidden = false
  IsoCount = 0
  IsoHidden = false
  IsoVisible = false
  LockPosition = false
  Perspective = false
  Rotation = 0
  Scale = 0.5
  ScaleType = 0
  SeamHidden = false
  SeamVisible = true
  SmoothHidden = false
  SmoothVisible = true
  X = 30.583
  XDirection = (0.707,0.707,0)
  Y = 183.107
FEATURE [TechDraw::DrawProjGroupItem] ProjItem007  label="Front002"
  CoarseView = false
  Direction = (1,-1e-16,0)
  Focus = 100
  HardHidden = false
  IsoCount = 0
  IsoHidden = false
  IsoVisible = false
  LockPosition = true
  Perspective = false
  Rotation = 0
  RotationVector = (1,0,0)
  ScaleType = 2
  SeamHidden = false
  SeamVisible = true
  SmoothHidden = false
  SmoothVisible = true
  Source = -> [Body021]
  Type = 0
  X = 0
  XDirection = (1e-16,1,0)
  Y = 0
FEATURE [TechDraw::DrawProjGroupItem] ProjItem008  label="Left001"
  CoarseView = false
  Direction = (0,-1,0)
  Focus = 100
  HardHidden = false
  IsoCount = 0
  IsoHidden = false
  IsoVisible = false
  LockPosition = true
  Perspective = false
  Rotation = 0
  RotationVector = (1,0,0)
  ScaleType = 2
  SeamHidden = false
  SeamVisible = true
  SmoothHidden = false
  SmoothVisible = true
  Source = -> [Body021]
  Type = 1
  X = 65
  XDirection = (1,0,0)
  Y = 0
FEATURE [TechDraw::DrawProjGroupItem] ProjItem009  label="Rear"
  CoarseView = false
  Direction = (-1,1e-16,0)
  Focus = 100
  HardHidden = false
  IsoCount = 0
  IsoHidden = false
  IsoVisible = false
  LockPosition = true
  Perspective = false
  Rotation = 0
  RotationVector = (1,0,0)
  ScaleType = 2
  SeamHidden = false
  SeamVisible = true
  SmoothHidden = false
  SmoothVisible = true
  Source = -> [Body021]
  Type = 3
  X = 130
  XDirection = (-1e-16,-1,0)
  Y = 0
FEATURE [TechDraw::DrawProjGroupItem] ProjItem010  label="Right001"
  CoarseView = false
  Direction = (2e-16,1,0)
  Focus = 100
  HardHidden = false
  IsoCount = 0
  IsoHidden = false
  IsoVisible = false
  LockPosition = true
  Perspective = false
  Rotation = 0
  RotationVector = (1,0,0)
  ScaleType = 2
  SeamHidden = false
  SeamVisible = true
  SmoothHidden = false
  SmoothVisible = true
  Source = -> [Body021]
  Type = 2
  X = -65
  XDirection = (-1,2e-16,0)
  Y = 0
FEATURE [TechDraw::DrawProjGroupItem] ProjItem012  label="Top"
  CoarseView = false
  Direction = (0,0,1)
  Focus = 100
  HardHidden = false
  IsoCount = 0
  IsoHidden = false
  IsoVisible = false
  LockPosition = true
  Perspective = false
  Rotation = 0
  RotationVector = (1,0,0)
  ScaleType = 2
  SeamHidden = false
  SeamVisible = true
  SmoothHidden = false
  SmoothVisible = true
  Source = -> [Body021]
  Type = 4
  X = 0
  XDirection = (1e-16,1,0)
  Y = -70.3637
FEATURE [TechDraw::DrawProjGroupItem] ProjItem013  label="Bottom002"
  CoarseView = false
  Direction = (0,0,-1)
  Focus = 100
  HardHidden = false
  IsoCount = 0
  IsoHidden = false
  IsoVisible = false
  LockPosition = false
  Perspective = false
  Rotation = 0
  RotationVector = (1,0,0)
  ScaleType = 2
  SeamHidden = false
  SeamVisible = true
  SmoothHidden = false
  SmoothVisible = true
  Source = -> [Body021]
  Type = 5
  X = 0
  XDirection = (1e-16,1,0)
  Y = 15
FEATURE [TechDraw::DrawProjGroup] ProjGroup002
  Anchor = -> ProjItem007
  AutoDistribute = true
  LockPosition = false
  ProjectionType = 0
  Rotation = 0
  ScaleType = 0
  Source = -> [Body021]
  Views = -> [ProjItem007,ProjItem008,ProjItem009,ProjItem010,ProjItem012,ProjItem013]
  X = 103.639
  Y = 118.803
  spacingX = 15
  spacingY = 15
FEATURE [TechDraw::DrawViewDimension] Dimension024
  Arbitrary = false
  ArbitraryTolerances = false
  EqualTolerance = false
  FormatSpec = R%.2f
  FormatSpecOverTolerance = %+.2f
  FormatSpecUnderTolerance = %+.2f
  Inverted = false
  LockPosition = false
  MeasureType = 1
  OverTolerance = 0
  References2D = -> [ProjItem013]
  Rotation = 0
  ScaleType = 0
  TheoreticalExact = false
  Type = 4
  UnderTolerance = 0
  X = 19.1509
  Y = 14.0701
FEATURE [TechDraw::DrawViewDimension] Dimension025
  Arbitrary = false
  ArbitraryTolerances = false
  EqualTolerance = false
  FormatSpec = %.2f
  FormatSpecOverTolerance = %+.2f
  FormatSpecUnderTolerance = %+.2f
  Inverted = false
  LockPosition = false
  MeasureType = 1
  OverTolerance = 0
  References2D = -> [ProjItem013]
  Rotation = 0
  ScaleType = 0
  TheoreticalExact = false
  Type = 2
  UnderTolerance = 0
  X = -34.234
  Y = -0.195417
FEATURE [TechDraw::DrawViewDimension] Dimension026
  Arbitrary = false
  ArbitraryTolerances = false
  EqualTolerance = false
  FormatSpec = %.2f
  FormatSpecOverTolerance = %+.2f
  FormatSpecUnderTolerance = %+.2f
  Inverted = false
  LockPosition = false
  MeasureType = 1
  OverTolerance = 0
  References2D = -> [ProjItem013]
  Rotation = 0
  ScaleType = 0
  TheoreticalExact = false
  Type = 1
  UnderTolerance = 0
  X = -0.586252
  Y = -21.9856
FEATURE [TechDraw::DrawViewDimension] Dimension028
  Arbitrary = false
  ArbitraryTolerances = false
  EqualTolerance = false
  FormatSpec = %.2f
  FormatSpecOverTolerance = %+.2f
  FormatSpecUnderTolerance = %+.2f
  Inverted = false
  LockPosition = false
  MeasureType = 1
  OverTolerance = 0
  References2D = -> [ProjItem013]
  Rotation = 0
  ScaleType = 0
  TheoreticalExact = false
  Type = 1
  UnderTolerance = 0
  X = -16.2817
  Y = 7.29445
FEATURE [TechDraw::DrawViewDimension] Dimension029
  Arbitrary = false
  ArbitraryTolerances = false
  EqualTolerance = false
  FormatSpec = %.2f
  FormatSpecOverTolerance = %+.2f
  FormatSpecUnderTolerance = %+.2f
  Inverted = false
  LockPosition = false
  MeasureType = 1
  OverTolerance = 0
  References2D = -> [ProjItem013]
  Rotation = 0
  ScaleType = 0
  TheoreticalExact = false
  Type = 2
  UnderTolerance = 0
  X = 28.5566
  Y = -6.20621
FEATURE [TechDraw::DrawViewDimension] Dimension030
  Arbitrary = false
  ArbitraryTolerances = false
  EqualTolerance = false
  FormatSpec = %.2f
  FormatSpecOverTolerance = %+.2f
  FormatSpecUnderTolerance = %+.2f
  Inverted = false
  LockPosition = false
  MeasureType = 1
  OverTolerance = 0
  References2D = -> [ProjItem013]
  Rotation = 0
  ScaleType = 0
  TheoreticalExact = false
  Type = 1
  UnderTolerance = 0
  X = 37.3578
  Y = 3.61298
FEATURE [TechDraw::DrawViewDimension] Dimension031
  Arbitrary = false
  ArbitraryTolerances = false
  EqualTolerance = false
  FormatSpec = %.2f
  FormatSpecOverTolerance = %+.2f
  FormatSpecUnderTolerance = %+.2f
  Inverted = false
  LockPosition = false
  MeasureType = 1
  OverTolerance = 0
  References2D = -> [ProjItem008]
  Rotation = 0
  ScaleType = 0
  TheoreticalExact = false
  Type = 1
  UnderTolerance = 0
  X = -5.76623
  Y = 0.287702
FEATURE [TechDraw::DrawViewDimension] Dimension032
  Arbitrary = false
  ArbitraryTolerances = false
  EqualTolerance = false
  FormatSpec = %.2f
  FormatSpecOverTolerance = %+.2f
  FormatSpecUnderTolerance = %+.2f
  Inverted = false
  LockPosition = false
  MeasureType = 1
  OverTolerance = 0
  References2D = -> [ProjItem008]
  Rotation = 0
  ScaleType = 0
  TheoreticalExact = false
  Type = 2
  UnderTolerance = 0
  X = -0.901396
  Y = 15.1348
FEATURE [TechDraw::DrawViewDimension] Dimension033
  Arbitrary = false
  ArbitraryTolerances = false
  EqualTolerance = false
  FormatSpec = %.2f
  FormatSpecOverTolerance = %+.2f
  FormatSpecUnderTolerance = %+.2f
  Inverted = false
  LockPosition = false
  MeasureType = 1
  OverTolerance = 0
  References2D = -> [ProjItem008]
  Rotation = 0
  ScaleType = 0
  TheoreticalExact = false
  Type = 2
  UnderTolerance = 0
  X = 21.8895
  Y = -17.5
FEATURE [TechDraw::DrawViewDimension] Dimension035
  Arbitrary = false
  ArbitraryTolerances = false
  EqualTolerance = false
  FormatSpec = %.2f
  FormatSpecOverTolerance = %+.2f
  FormatSpecUnderTolerance = %+.2f
  Inverted = false
  LockPosition = false
  MeasureType = 1
  OverTolerance = 0
  References2D = -> [ProjItem009]
  Rotation = 0
  ScaleType = 0
  TheoreticalExact = false
  Type = 2
  UnderTolerance = 0
  X = 28.1125
  Y = -31.9901
FEATURE [TechDraw::DrawViewDimension] Dimension036
  Arbitrary = false
  ArbitraryTolerances = false
  EqualTolerance = false
  FormatSpec = %.2f
  FormatSpecOverTolerance = %+.2f
  FormatSpecUnderTolerance = %+.2f
  Inverted = false
  LockPosition = false
  MeasureType = 1
  OverTolerance = 0
  References2D = -> [ProjItem009]
  Rotation = 0
  ScaleType = 0
  TheoreticalExact = false
  Type = 1
  UnderTolerance = 0
  X = 12.1513
  Y = -8.7684
FEATURE [TechDraw::DrawViewDimension] Dimension037
  Arbitrary = false
  ArbitraryTolerances = false
  EqualTolerance = false
  FormatSpec = %.2f
  FormatSpecOverTolerance = %+.2f
  FormatSpecUnderTolerance = %+.2f
  Inverted = false
  LockPosition = false
  MeasureType = 1
  OverTolerance = 0
  References2D = -> [ProjItem009]
  Rotation = 0
  ScaleType = 0
  TheoreticalExact = false
  Type = 2
  UnderTolerance = 0
  X = 1.14094
  Y = -29.3403
FEATURE [TechDraw::DrawViewDimension] Dimension038
  Arbitrary = false
  ArbitraryTolerances = false
  EqualTolerance = false
  FormatSpec = %.2f
  FormatSpecOverTolerance = %+.2f
  FormatSpecUnderTolerance = %+.2f
  Inverted = false
  LockPosition = false
  MeasureType = 1
  OverTolerance = 0
  References2D = -> [ProjItem009]
  Rotation = 0
  ScaleType = 0
  TheoreticalExact = false
  Type = 2
  UnderTolerance = 0
  X = -34.6499
  Y = -0.866784
FEATURE [TechDraw::DrawViewDimension] Dimension039
  Arbitrary = false
  ArbitraryTolerances = false
  EqualTolerance = false
  FormatSpec = %.2f
  FormatSpecOverTolerance = %+.2f
  FormatSpecUnderTolerance = %+.2f
  Inverted = false
  LockPosition = false
  MeasureType = 1
  OverTolerance = 0
  References2D = -> [ProjItem009]
  Rotation = 0
  ScaleType = 0
  TheoreticalExact = false
  Type = 1
  UnderTolerance = 0
  X = 18.4523
  Y = 34.8435
FEATURE [TechDraw::DrawViewDimension] Dimension040
  Arbitrary = false
  ArbitraryTolerances = false
  EqualTolerance = false
  FormatSpec = %.2f
  FormatSpecOverTolerance = %+.2f
  FormatSpecUnderTolerance = %+.2f
  Inverted = false
  LockPosition = false
  MeasureType = 1
  OverTolerance = 0
  References2D = -> [ProjItem009]
  Rotation = 0
  ScaleType = 0
  TheoreticalExact = false
  Type = 1
  UnderTolerance = 0
  X = -5.41184
  Y = 32.4516
FEATURE [TechDraw::DrawViewDimension] Dimension042
  Arbitrary = false
  ArbitraryTolerances = false
  EqualTolerance = false
  FormatSpec = %.2f
  FormatSpecOverTolerance = %+.2f
  FormatSpecUnderTolerance = %+.2f
  Inverted = false
  LockPosition = false
  MeasureType = 1
  OverTolerance = 0
  References2D = -> [ProjItem012]
  Rotation = 0
  ScaleType = 0
  TheoreticalExact = false
  Type = 2
  UnderTolerance = 0
  X = -29.4955
  Y = 11.4157
FEATURE [TechDraw::DrawViewDimension] Dimension043
  Arbitrary = false
  ArbitraryTolerances = false
  EqualTolerance = false
  FormatSpec = %.2f
  FormatSpecOverTolerance = %+.2f
  FormatSpecUnderTolerance = %+.2f
  Inverted = false
  LockPosition = false
  MeasureType = 1
  OverTolerance = 0
  References2D = -> [ProjItem012]
  Rotation = 0
  ScaleType = 0
  TheoreticalExact = false
  Type = 2
  UnderTolerance = 0
  X = -36.1103
  Y = 7.53454
FEATURE [TechDraw::DrawViewDimension] Dimension044
  Arbitrary = false
  ArbitraryTolerances = false
  EqualTolerance = false
  FormatSpec = %.2f
  FormatSpecOverTolerance = %+.2f
  FormatSpecUnderTolerance = %+.2f
  Inverted = false
  LockPosition = false
  MeasureType = 1
  OverTolerance = 0
  References2D = -> [ProjItem012]
  Rotation = 0
  ScaleType = 0
  TheoreticalExact = false
  Type = 2
  UnderTolerance = 0
  X = -42.6347
  Y = 2.67713
FEATURE [TechDraw::DrawViewDimension] Dimension045
  Arbitrary = false
  ArbitraryTolerances = false
  EqualTolerance = false
  FormatSpec = %.2f
  FormatSpecOverTolerance = %+.2f
  FormatSpecUnderTolerance = %+.2f
  Inverted = false
  LockPosition = false
  MeasureType = 1
  OverTolerance = 0
  References2D = -> [ProjItem012]
  Rotation = 0
  ScaleType = 0
  TheoreticalExact = false
  Type = 1
  UnderTolerance = 0
  X = -14.7458
  Y = 24.3035
FEATURE [TechDraw::DrawViewDimension] Dimension046
  Arbitrary = false
  ArbitraryTolerances = false
  EqualTolerance = false
  FormatSpec = %.2f
  FormatSpecOverTolerance = %+.2f
  FormatSpecUnderTolerance = %+.2f
  Inverted = false
  LockPosition = false
  MeasureType = 1
  OverTolerance = 0
  References2D = -> [ProjItem012]
  Rotation = 0
  ScaleType = 0
  TheoreticalExact = false
  Type = 1
  UnderTolerance = 0
  X = -15.4599
  Y = -23.8107
FEATURE [TechDraw::DrawViewDimension] Dimension047
  Arbitrary = false
  ArbitraryTolerances = false
  EqualTolerance = false
  FormatSpec = %.2f
  FormatSpecOverTolerance = %+.2f
  FormatSpecUnderTolerance = %+.2f
  Inverted = false
  LockPosition = false
  MeasureType = 1
  OverTolerance = 0
  References2D = -> [ProjItem012]
  Rotation = 0
  ScaleType = 0
  TheoreticalExact = false
  Type = 1
  UnderTolerance = 0
  X = -8.2936
  Y = -30.4726
FEATURE [TechDraw::DrawViewDimension] Dimension048
  Arbitrary = false
  ArbitraryTolerances = false
  EqualTolerance = false
  FormatSpec = %.2f
  FormatSpecOverTolerance = %+.2f
  FormatSpecUnderTolerance = %+.2f
  Inverted = false
  LockPosition = false
  MeasureType = 1
  OverTolerance = 0
  References2D = -> [ProjItem007]
  Rotation = 0
  ScaleType = 0
  TheoreticalExact = false
  Type = 2
  UnderTolerance = 0
  X = -34.5365
  Y = -11.6191
FEATURE [TechDraw::DrawViewDimension] Dimension049
  Arbitrary = false
  ArbitraryTolerances = false
  EqualTolerance = false
  FormatSpec = %.2f
  FormatSpecOverTolerance = %+.2f
  FormatSpecUnderTolerance = %+.2f
  Inverted = false
  LockPosition = false
  MeasureType = 1
  OverTolerance = 0
  References2D = -> [ProjItem008]
  Rotation = 0
  ScaleType = 0
  TheoreticalExact = false
  Type = 2
  UnderTolerance = 0
  X = -24.7797
  Y = -13.3181
FEATURE [TechDraw::DrawViewDimension] Dimension050
  Arbitrary = false
  ArbitraryTolerances = false
  EqualTolerance = false
  FormatSpec = %.2f
  FormatSpecOverTolerance = %+.2f
  FormatSpecUnderTolerance = %+.2f
  Inverted = false
  LockPosition = false
  MeasureType = 1
  OverTolerance = 0
  References2D = -> [ProjItem007]
  Rotation = 0
  ScaleType = 0
  TheoreticalExact = false
  Type = 2
  UnderTolerance = 0
  X = -41.5171
  Y = -22.3563
FEATURE [TechDraw::DrawViewDimension] Dimension051
  Arbitrary = false
  ArbitraryTolerances = false
  EqualTolerance = false
  FormatSpec = %.2f
  FormatSpecOverTolerance = %+.2f
  FormatSpecUnderTolerance = %+.2f
  Inverted = false
  LockPosition = false
  MeasureType = 1
  OverTolerance = 0
  References2D = -> [ProjItem007]
  Rotation = 0
  ScaleType = 0
  TheoreticalExact = false
  Type = 1
  UnderTolerance = 0
  X = 6.60144
  Y = -35.5375
FEATURE [TechDraw::DrawViewDimension] Dimension052
  Arbitrary = false
  ArbitraryTolerances = false
  EqualTolerance = false
  FormatSpec = %.2f
  FormatSpecOverTolerance = %+.2f
  FormatSpecUnderTolerance = %+.2f
  Inverted = false
  LockPosition = false
  MeasureType = 1
  OverTolerance = 0
  References2D = -> [ProjItem007]
  Rotation = 0
  ScaleType = 0
  TheoreticalExact = false
  Type = 1
  UnderTolerance = 0
  X = 6.19512
  Y = -28.64
FEATURE [TechDraw::DrawViewAnnotation] Annotation
  Font = Sans Serif
  LineSpace = 80
  LockPosition = false
  MaxWidth = -1
  Rotation = 0
  ScaleType = 0
  Text = Drill 3/16" - Depth 27.0 mm | Drill 5mm - Depth 11.0 mm | Tap M6x1.0 | Countersink to match M6 plug
  TextSize = 2.5
  TextStyle = 0
  X = 243.063
  Y = 71.5534
FEATURE [TechDraw::DrawViewDimension] Dimension053
  Arbitrary = false
  ArbitraryTolerances = false
  EqualTolerance = false
  FormatSpec = %.2f
  FormatSpecOverTolerance = %+.2f
  FormatSpecUnderTolerance = %+.2f
  Inverted = false
  LockPosition = false
  MeasureType = 1
  OverTolerance = 0
  References2D = -> [ProjItem010]
  Rotation = 0
  ScaleType = 0
  TheoreticalExact = false
  Type = 2
  UnderTolerance = 0
  X = -25.1679
  Y = -21.1101
FEATURE [TechDraw::DrawViewDimension] Dimension054
  Arbitrary = false
  ArbitraryTolerances = false
  EqualTolerance = false
  FormatSpec = %.2f
  FormatSpecOverTolerance = %+.2f
  FormatSpecUnderTolerance = %+.2f
  Inverted = false
  LockPosition = false
  MeasureType = 1
  OverTolerance = 0
  References2D = -> [ProjItem010]
  Rotation = 0
  ScaleType = 0
  TheoreticalExact = false
  Type = 1
  UnderTolerance = 0
  X = 2.56697
  Y = -35.7193
FEATURE [TechDraw::DrawViewDimension] Dimension055
  Arbitrary = false
  ArbitraryTolerances = false
  EqualTolerance = false
  FormatSpec = %.2f
  FormatSpecOverTolerance = %+.2f
  FormatSpecUnderTolerance = %+.2f
  Inverted = false
  LockPosition = false
  MeasureType = 1
  OverTolerance = 0
  References2D = -> [ProjItem010]
  Rotation = 0
  ScaleType = 0
  TheoreticalExact = false
  Type = 1
  UnderTolerance = 0
  X = -15.1824
  Y = -41.0119
FEATURE [TechDraw::DrawViewAnnotation] Annotation001
  Font = Sans Serif
  LineSpace = 80
  LockPosition = false
  MaxWidth = -1
  Rotation = 0
  ScaleType = 0
  Text = Drill 3/16" - Depth 32.0mm | Drill 5.0mm - Depth 7.3mm | Tap M6x1.0
  TextSize = 2.5
  TextStyle = 0
  X = 31.0661
  Y = 115.642
FEATURE [TechDraw::DrawViewAnnotation] Annotation002
  Font = Sans Serif
  LineSpace = 80
  LockPosition = false
  MaxWidth = -1
  Rotation = 0
  ScaleType = 0
  Text = Through Drill 1/8" & tap M4x0.7
  TextSize = 2.5
  TextStyle = 0
  X = 153.114
  Y = 56.3806
FEATURE [TechDraw::DrawViewAnnotation] Annotation003
  Font = Sans Serif
  LineSpace = 80
  LockPosition = false
  MaxWidth = -1
  Rotation = 0
  ScaleType = 0
  Text = Drill 5/64" - Depth 6.0mm | Tap M2.5x0.45
  TextSize = 2.5
  TextStyle = 0
  X = 151.717
  Y = 30.2802
FEATURE [TechDraw::DrawViewAnnotation] Annotation004
  Font = Sans Serif
  LineSpace = 80
  LockPosition = false
  MaxWidth = -1
  Rotation = 0
  ScaleType = 0
  Text = Drill 7.20mm | Counterbore 12.0mm | Depth 2.18mm
  TextSize = 2.5
  TextStyle = 0
  X = 106.454
  Y = 149.635
FEATURE [TechDraw::DrawViewDimension] Dimension056
  Arbitrary = false
  ArbitraryTolerances = false
  EqualTolerance = false
  FormatSpec = %.2f
  FormatSpecOverTolerance = %+.2f
  FormatSpecUnderTolerance = %+.2f
  Inverted = false
  LockPosition = false
  MeasureType = 1
  OverTolerance = 0
  References2D = -> [ProjItem007]
  Rotation = 0
  ScaleType = 0
  TheoreticalExact = false
  Type = 2
  UnderTolerance = 0
  X = 28.3752
  Y = 1.21565
FEATURE [TechDraw::DrawViewAnnotation] Annotation005
  Font = Sans Serif
  LineSpace = 80
  LockPosition = false
  MaxWidth = -1
  Rotation = 0
  ScaleType = 0
  Text = Through-drill 3/32" & tap M3x0.5
  TextSize = 2.5
  TextStyle = 0
  X = 236.033
  Y = 126.03
FEATURE [TechDraw::DrawViewAnnotation] Annotation006
  Font = Sans Serif
  LineSpace = 80
  LockPosition = false
  MaxWidth = -1
  Rotation = 0
  ScaleType = 0
  Text = Drill 5/32" - Depth 10.0mm | Tap M5x0.8
  TextSize = 2.5
  TextStyle = 0
  X = 204.142
  Y = 82.1491
FEATURE [TechDraw::DrawViewDimension] Dimension057
  Arbitrary = false
  ArbitraryTolerances = false
  EqualTolerance = false
  FormatSpec = %.2f
  FormatSpecOverTolerance = %+.2f
  FormatSpecUnderTolerance = %+.2f
  Inverted = false
  LockPosition = false
  MeasureType = 1
  OverTolerance = 0
  References2D = -> [ProjItem007]
  Rotation = 0
  ScaleType = 0
  TheoreticalExact = false
  Type = 1
  UnderTolerance = 0
  X = -14.2126
  Y = 0.579442
FEATURE [TechDraw::DrawViewDimension] Dimension058
  Arbitrary = false
  ArbitraryTolerances = false
  EqualTolerance = false
  FormatSpec = %.2f
  FormatSpecOverTolerance = %+.2f
  FormatSpecUnderTolerance = %+.2f
  Inverted = false
  LockPosition = false
  MeasureType = 1
  OverTolerance = 0
  References2D = -> [ProjItem007]
  Rotation = 0
  ScaleType = 0
  TheoreticalExact = false
  Type = 2
  UnderTolerance = 0
  X = 16.8932
  Y = -8.86083
FEATURE [TechDraw::DrawViewDimension] Dimension059
  Arbitrary = false
  ArbitraryTolerances = false
  EqualTolerance = false
  FormatSpec = %.2f
  FormatSpecOverTolerance = %+.2f
  FormatSpecUnderTolerance = %+.2f
  Inverted = false
  LockPosition = false
  MeasureType = 1
  OverTolerance = 0
  References2D = -> [ProjItem009]
  Rotation = 0
  ScaleType = 0
  TheoreticalExact = false
  Type = 1
  UnderTolerance = 0
  X = 12.9638
  Y = -1.97335
FEATURE [TechDraw::DrawLeaderLine] LeaderLine
  AutoHorizontal = true
  EndSymbol = 7
  LeaderParent = -> ProjItem009
  LockPosition = true
  Rotation = 0
  Scalable = false
  ScaleType = 0
  StartSymbol = 0
  WayPoints = (3) [(0,0,0),(-224.773,-77.6001,0),(-166.796,-77.6001,0)]
  X = -1.79941
  Y = 0.349869
FEATURE [TechDraw::DrawLeaderLine] LeaderLine001
  AutoHorizontal = true
  EndSymbol = 7
  LeaderParent = -> ProjItem009
  LockPosition = true
  Rotation = 0
  Scalable = false
  ScaleType = 0
  StartSymbol = 0
  WayPoints = (3) [(0,0,0),(-68.577,183.451,0),(-97.1196,183.451,0)]
  X = -2.70674
  Y = -16.5506
FEATURE [TechDraw::DrawLeaderLine] LeaderLine002
  AutoHorizontal = true
  EndSymbol = 7
  LeaderParent = -> ProjItem009
  LockPosition = true
  Rotation = 0
  Scalable = false
  ScaleType = 0
  StartSymbol = 0
  WayPoints = (3) [(0,0,0),(80.2759,208.717,0),(72.2586,208.717,0)]
  X = 18.4429
  Y = -22.4083
FEATURE [TechDraw::DrawLeaderLine] LeaderLine003
  AutoHorizontal = true
  EndSymbol = 7
  LeaderParent = -> ProjItem007
  LockPosition = true
  Rotation = 0
  Scalable = false
  ScaleType = 0
  StartSymbol = 0
  WayPoints = (3) [(0,0,0),(130.582,-100.612,0),(28.8993,-100.612,0)]
  X = 15.0953
  Y = 21.8222
FEATURE [TechDraw::DrawLeaderLine] LeaderLine004
  AutoHorizontal = true
  EndSymbol = 7
  LeaderParent = -> ProjItem010
  LockPosition = true
  Rotation = 0
  Scalable = false
  ScaleType = 0
  StartSymbol = 0
  WayPoints = (3) [(0,0,0),(160.242,-169.036,0),(48.8544,-169.036,0)]
  X = 6.30669
  Y = -17.0626
FEATURE [TechDraw::DrawLeaderLine] LeaderLine005
  AutoHorizontal = true
  EndSymbol = 7
  LeaderParent = -> ProjItem012
  LockPosition = true
  Rotation = 0
  Scalable = false
  ScaleType = 0
  StartSymbol = 0
  WayPoints = (3) [(0,0,0),(55.2298,-68.074,0),(346.792,-68.074,0)]
  X = -5.81726
  Y = 1.79244
FEATURE [TechDraw::DrawLeaderLine] LeaderLine006
  AutoHorizontal = true
  EndSymbol = 7
  LeaderParent = -> ProjItem012
  LockPosition = true
  Rotation = 0
  Scalable = false
  ScaleType = 0
  StartSymbol = 0
  WayPoints = (3) [(0,0,0),(83.487,113.029,0),(211.928,113.029,0)]
  X = 9.21039
  Y = -5.91405
FEATURE [TechDraw::DrawViewDimension] Dimension060
  Arbitrary = false
  ArbitraryTolerances = false
  EqualTolerance = false
  FormatSpec = %.2f
  FormatSpecOverTolerance = %+.2f
  FormatSpecUnderTolerance = %+.2f
  Inverted = false
  LockPosition = false
  MeasureType = 1
  OverTolerance = 0
  References2D = -> [ProjItem013]
  Rotation = 0
  ScaleType = 0
  TheoreticalExact = false
  Type = 2
  UnderTolerance = 0
  X = -15.7965
  Y = -8.8593
FEATURE [TechDraw::DrawLeaderLine] LeaderLine007
  AutoHorizontal = true
  EndSymbol = 7
  LeaderParent = -> ProjItem012
  LockPosition = true
  Rotation = 0
  Scalable = false
  ScaleType = 0
  StartSymbol = 0
  WayPoints = (3) [(0,0,0),(-136.48,122.41,0),(-289.843,122.41,0)]
  X = -16.9452
  Y = -11.0576
FEATURE [TechDraw::DrawViewAnnotation] Annotation007
  Font = Sans Serif
  LineSpace = 80
  LockPosition = false
  MaxWidth = -1
  Rotation = 0
  ScaleType = 0
  Text = Pocket to provide clearance |  for Hemera Heatbreak | Depth 4.0mm
  TextSize = 2.5
  TextStyle = 0
  X = 45.3136
  Y = 24.4432
FEATURE [TechDraw::DrawViewDimension] Dimension061
  Arbitrary = false
  ArbitraryTolerances = false
  EqualTolerance = false
  FormatSpec = %.2f
  FormatSpecOverTolerance = %+.2f
  FormatSpecUnderTolerance = %+.2f
  Inverted = false
  LockPosition = false
  MeasureType = 1
  OverTolerance = 0
  References2D = -> [ProjItem012]
  Rotation = 0
  ScaleType = 0
  TheoreticalExact = false
  Type = 2
  UnderTolerance = 0
  X = 24.7033
  Y = 25.7597
FEATURE [TechDraw::DrawViewDimension] Dimension062
  Arbitrary = false
  ArbitraryTolerances = false
  EqualTolerance = false
  FormatSpec = %.2f
  FormatSpecOverTolerance = %+.2f
  FormatSpecUnderTolerance = %+.2f
  Inverted = false
  LockPosition = false
  MeasureType = 1
  OverTolerance = 0
  References2D = -> [ProjItem012]
  Rotation = 0
  ScaleType = 0
  TheoreticalExact = false
  Type = 2
  UnderTolerance = 0
  X = 18.2398
  Y = 26.1674
FEATURE [TechDraw::DrawViewDimension] Dimension063
  Arbitrary = false
  ArbitraryTolerances = false
  EqualTolerance = false
  FormatSpec = %.2f
  FormatSpecOverTolerance = %+.2f
  FormatSpecUnderTolerance = %+.2f
  Inverted = false
  LockPosition = false
  MeasureType = 1
  OverTolerance = 0
  References2D = -> [ProjItem012]
  Rotation = 0
  ScaleType = 0
  TheoreticalExact = false
  Type = 1
  UnderTolerance = 0
  X = -21.2141
  Y = -1.32694
FEATURE [TechDraw::DrawViewDimension] Dimension064
  Arbitrary = false
  ArbitraryTolerances = false
  EqualTolerance = false
  FormatSpec = %.2f
  FormatSpecOverTolerance = %+.2f
  FormatSpecUnderTolerance = %+.2f
  Inverted = false
  LockPosition = false
  MeasureType = 1
  OverTolerance = 0
  References2D = -> [ProjItem012]
  Rotation = 0
  ScaleType = 0
  TheoreticalExact = false
  Type = 1
  UnderTolerance = 0
  X = -8.89372
  Y = -7.61363
FEATURE [TechDraw::DrawLeaderLine] LeaderLine008
  AutoHorizontal = true
  EndSymbol = 7
  LeaderParent = -> ProjItem007
  LockPosition = true
  Rotation = 0
  Scalable = false
  ScaleType = 0
  StartSymbol = 0
  WayPoints = (3) [(0,0,0),(299.692,157.585,0),(353.158,157.585,0)]
  X = 1.42174
  Y = -17.8935
FEATURE [TechDraw::DrawViewAnnotation] Annotation008
  Font = Sans Serif
  LineSpace = 80
  LockPosition = false
  MaxWidth = -1
  Rotation = 0
  ScaleType = 0
  Text = Drill 3/32" - Depth 7.0mm | Tap M3x0.5
  TextSize = 2.5
  TextStyle = 0
  X = 156.865
  Y = 84.0309
FEATURE [TechDraw::DrawPage] Page002  label="watercooled_printhead_dwg"
  KeepUpdated = false
  NextBalloonIndex = 1
  ProjectionType = 0
  Template = -> Template002
  Views = -> [View002,ProjGroup002,Dimension024,Dimension025,Dimension026,Dimension028,Dimension029,Dimension030,Dimension031,Dimension032,Dimension033,Dimension035,Dimension036,Dimension037,Dimension038,Dimension039,Dimension040,Dimension042,Dimension043,Dimension044,Dimension045,Dimension046,Dimension047,Dimension048,Dimension049,Dimension050,Dimension051,Dimension052,Annotation,Dimension053,Dimension054,+27 more]
FEATURE [PartDesign::CoordinateSystem] LCS_1
  AttacherType = Attacher::AttachEngine3D
  MapMode = 11
  Placement = pos=(-14.17,-15,40.95) rot=(0.707107,0,0.707107;3.14159rad)
  Support = -> [Hole014]
FEATURE [PartDesign::CoordinateSystem] LCS_2
  AttacherType = Attacher::AttachEngine3D
  MapMode = 11
  Placement = pos=(-14.17,15,40.95) rot=(0.707107,0,0.707107;3.14159rad)
  Support = -> [Hole014]
FEATURE [PartDesign::CoordinateSystem] LCS_3
  AttacherType = Attacher::AttachEngine3D
  MapMode = 11
  Placement = pos=(-18.35,-16,5.5) rot=(0,-1,0;1.5708rad)
  Support = -> [Hole014]
FEATURE [PartDesign::CoordinateSystem] LCS_4
  AttacherType = Attacher::AttachEngine3D
  MapMode = 11
  Placement = pos=(6.35,12,5.5) rot=(0.57735,0.57735,0.57735;4.18879rad)
  Support = -> [Hole014]
FEATURE [PartDesign::CoordinateSystem] LCS_5
  AttacherType = Attacher::AttachEngine3D
  MapMode = 11
  Placement = pos=(-6.35,12,5.5) rot=(0.57735,0.57735,0.57735;4.18879rad)
  Support = -> [Hole014]
FEATURE [PartDesign::CoordinateSystem] LCS_6
  AttacherType = Attacher::AttachEngine3D
  MapMode = 11
  Placement = pos=(15.5,-3.95,15) rot=(0,0,1;1.5708rad)
  Support = -> [Hole014]
FEATURE [PartDesign::CoordinateSystem] LCS_7
  AttacherType = Attacher::AttachEngine3D
  MapMode = 11
  Placement = pos=(0,-6,1e-15) rot=(0.707107,0.707107,0;3.14159rad)
  Support = -> [Hole014]
FEATURE [PartDesign::CoordinateSystem] LCS_8
  AttacherType = Attacher::AttachEngine3D
  MapMode = 11
  Placement = pos=(-18.35,8e-15,9.05) rot=(0,-1,0;1.5708rad)
  Support = -> [Hole014]
FEATURE [PartDesign::CoordinateSystem] LCS_9
  AttacherType = Attacher::AttachEngine3D
  MapMode = 11
  Placement = pos=(-18.35,-15,40.95) rot=(0.707107,0,-0.707107;3.14159rad)
  Support = -> [Hole014]
FEATURE [PartDesign::CoordinateSystem] LCS_10
  AttacherType = Attacher::AttachEngine3D
  MapMode = 11
  Placement = pos=(-18.35,15,40.95) rot=(0.707107,0,-0.707107;3.14159rad)
  Support = -> [Hole014]
FEATURE [App::Part] Part  label="watercooled_block"
  Group = -> [Body021,LCS_1,LCS_2,LCS_3,LCS_4,LCS_5,LCS_6,LCS_7,LCS_8,LCS_9,LCS_10]
  Origin = -> Origin
